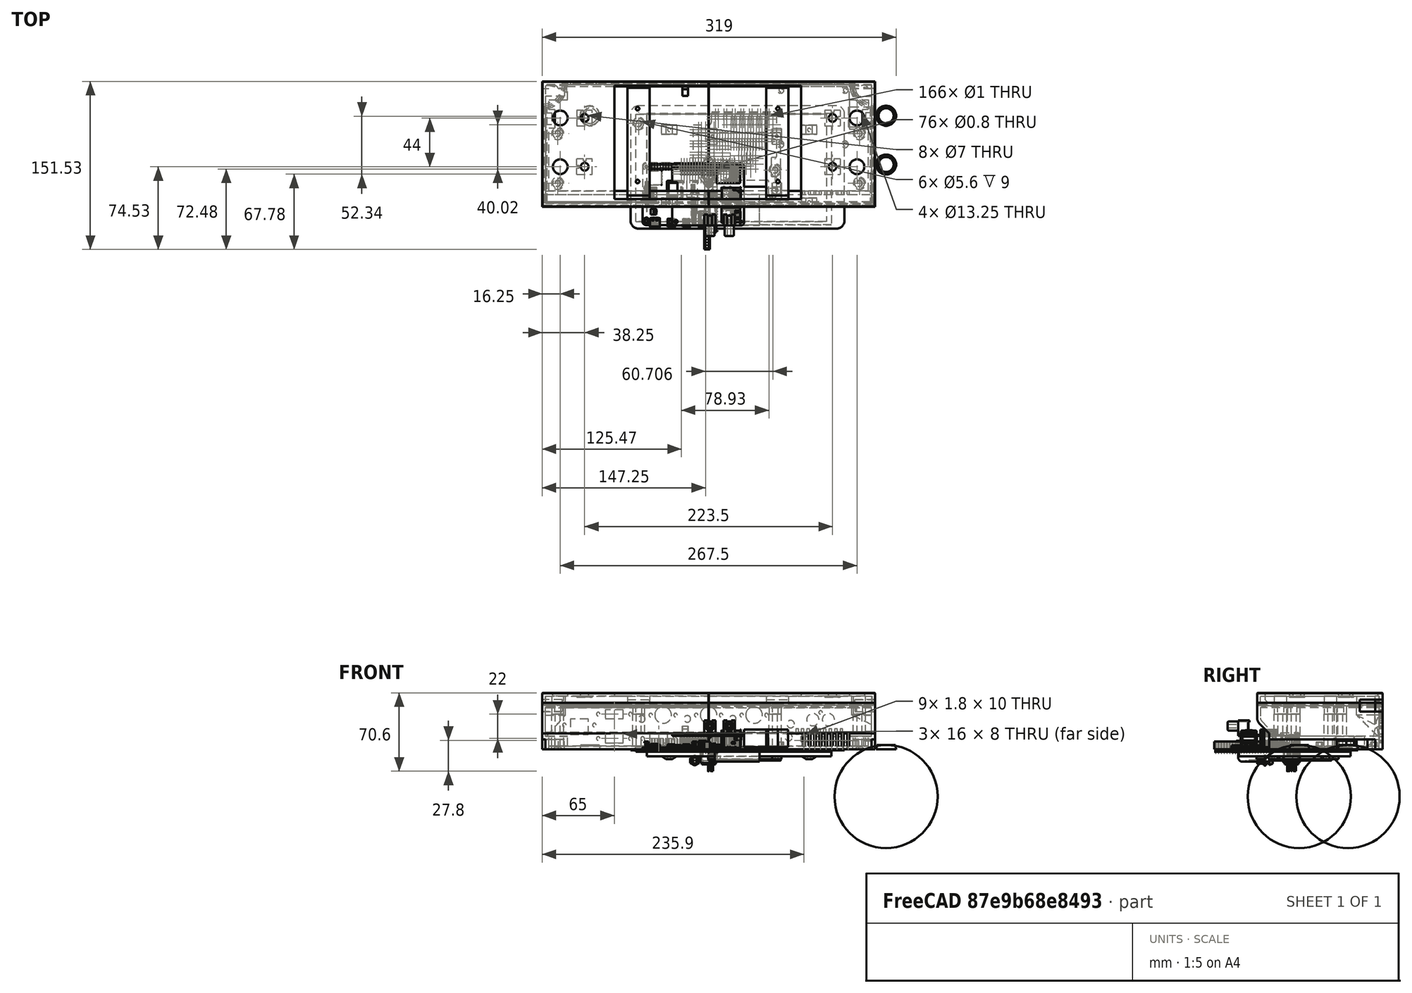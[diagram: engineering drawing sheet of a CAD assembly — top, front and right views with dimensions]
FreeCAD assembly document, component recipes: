
FREECAD ASSEMBLY — COMPONENT RECIPES ("MyZynthian-Boutique")

This assembly document has 19 components, labeled P0..P18 below (a component is one placed body or linked part). 12 of them carry a construction recipe — the FreeCAD feature program that regenerates the part from scratch, quoted from this document or its linked companion documents; the rest are supplied as boundary geometry only. No exploded tour is included for this assembly.
COMPONENT P0 — recipe-attached ("Body Bottom", modeled in this document).
Construction recipe (the document's own serialized feature program — sketch geometry with constraints, then the solid features built on it; lengths are millimeters unless a unit is written):

FEATURE [Sketcher::SketchObject] Sketch002
  FullyConstrained = true
  MapMode = 5
  Placement = pos=(0,0,0) rot=(0.57735,0.57735,0.57735;2.0944rad)
  Support = -> [YZ_Plane037]
  sketch-geometry (8):
    g0: LineSegment StartX=0 StartY=0 StartZ=0 EndX=102 EndY=0 EndZ=0
    g1: LineSegment StartX=102 StartY=0 StartZ=0 EndX=102 EndY=42 EndZ=0
    g2: LineSegment StartX=102 StartY=42 StartZ=0 EndX=-11 EndY=42 EndZ=0
    g3: LineSegment StartX=-11 StartY=42 StartZ=0 EndX=-11 EndY=28.3995 EndZ=0
    g4: LineSegment StartX=-8.94975 StartY=23.4497 StartZ=0 EndX=0 EndY=14.5 EndZ=0
    g5: LineSegment StartX=0 StartY=14.5 StartZ=0 EndX=0 EndY=0 EndZ=0
    g6: ArcOfCircle CenterX=-4 CenterY=28.3995 CenterZ=0 NormalX=0 NormalY=0 NormalZ=1 AngleXU=0 Radius=7 StartAngle=3.14159 EndAngle=3.92699
    g7: GeomPoint X=-11 Y=25.5 Z=0
  constraints (21):
    c: Coincident(g-1,g0)
    c: PointOnObject(g0,g-1)
    c: Coincident(g0,g1)
    c: Vertical(g1)
    c: Horizontal(g2)
    c: Coincident(g2,g3)
    c: Vertical(g3)
    c: PointOnObject(g4,g-2)
    c: Coincident(g4,g5)
    c: Coincident(g5,g0)
    c: DistanceX(g0,g0) = 102
    c: DistanceY(g1,g1) = 42
    c: DistanceY(g5,g5) = 14.5
    c: Angle(g4,g5) = 2.35619
    c: DistanceX(g2,g1) = 113
    c: PointOnObject(g7,g3)
    c: PointOnObject(g7,g4)
    c: Tangent(g3,g6) = -1.5708
    c: Tangent(g4,g6) = -1.5708
    c: Radius(g6) = 7
    c: Coincident(g2,g1)
FEATURE [PartDesign::Pad] Pad001  label="Base"
  Direction = (1,-2e-16,3e-16)
  Length = 300
  Length2 = 10
  Midplane = true
  Placement = pos=(0,0,0) rot=(0.57735,0.57735,0.57735;2.0944rad)
  Profile = -> Sketch002
  ReferenceAxis = -> Sketch002 [N_Axis]
  Type = 0
FEATURE [Sketcher::SketchObject] Sketch003
  ExternalGeometry = -> [Pad001]
  FullyConstrained = true
  MapMode = 5
  Placement = pos=(0,0,4e-16) rot=(0.707107,0.707107,0;3.14159rad)
  Support = -> [Pad001]
  sketch-geometry (20):
    g0: LineSegment StartX=95.5 StartY=130 StartZ=0 EndX=88.5 EndY=130 EndZ=0
    g1: LineSegment StartX=88.5 StartY=130 StartZ=0 EndX=88.5 EndY=147 EndZ=0
    g2: LineSegment StartX=88.5 StartY=147 StartZ=0 EndX=73.5 EndY=147 EndZ=0
    g3: LineSegment StartX=73.5 StartY=147 StartZ=0 EndX=73.5 EndY=141.5 EndZ=0
    g4: LineSegment StartX=73.5 StartY=141.5 StartZ=0 EndX=63 EndY=141.5 EndZ=0
    g5: LineSegment StartX=63 StartY=141.5 StartZ=0 EndX=63 EndY=147 EndZ=0
    g6: LineSegment StartX=63 StartY=147 StartZ=0 EndX=-2.84e-14 EndY=147 EndZ=0
    g7: LineSegment StartX=-2.84e-14 StartY=147 StartZ=0 EndX=-3.21e-14 EndY=150 EndZ=0
    g8: LineSegment StartX=-3.21e-14 StartY=150 StartZ=0 EndX=95.5 EndY=150 EndZ=0
    g9: LineSegment StartX=95.5 StartY=150 StartZ=0 EndX=95.5 EndY=130 EndZ=0
    g10: LineSegment StartX=95.5 StartY=-130 StartZ=0 EndX=88.5 EndY=-130 EndZ=0
    g11: LineSegment StartX=88.5 StartY=-130 StartZ=0 EndX=88.5 EndY=-147 EndZ=0
    g12: LineSegment StartX=88.5 StartY=-147 StartZ=0 EndX=73.5 EndY=-147 EndZ=0
    g13: LineSegment StartX=73.5 StartY=-147 StartZ=0 EndX=73.5 EndY=-141.5 EndZ=0
    g14: LineSegment StartX=73.5 StartY=-141.5 StartZ=0 EndX=63 EndY=-141.5 EndZ=0
    g15: LineSegment StartX=63 StartY=-141.5 StartZ=0 EndX=63 EndY=-147 EndZ=0
    g16: LineSegment StartX=63 StartY=-147 StartZ=0 EndX=3.55e-14 EndY=-147 EndZ=0
    g17: LineSegment StartX=3.55e-14 StartY=-147 StartZ=0 EndX=3.37e-14 EndY=-150 EndZ=0
    g18: LineSegment StartX=3.37e-14 StartY=-150 StartZ=0 EndX=95.5 EndY=-150 EndZ=0
    g19: LineSegment StartX=95.5 StartY=-150 StartZ=0 EndX=95.5 EndY=-130 EndZ=0
  constraints (58):
    c: Coincident(g0,g1)
    c: Horizontal(g2)
    c: Coincident(g2,g3)
    c: Coincident(g3,g4)
    c: Horizontal(g4)
    c: Coincident(g4,g5)
    c: Vertical(g5)
    c: Coincident(g5,g6)
    c: PointOnObject(g6,g-5)
    c: Horizontal(g6)
    c: Coincident(g6,g7)
    c: Vertical(g3)
    c: Vertical(g1)
    c: Horizontal(g0)
    c: DistanceY(g7,g7) = 3
    c: Horizontal(g5,g2)
    c: DistanceX(g5,g2) = 10.5
    c: Coincident(g8,g7)
    c: Horizontal(g8)
    c: DistanceX(g2,g-4) = 28.5
    c: DistanceY(g5,g5) = 5.5
    c: Coincident(g7,g-5)
    c: DistanceY(g0,g8) = 20
    c: DistanceX(g8,g-4) = 6.5
    c: DistanceX(g0,g0) = 7
    c: Coincident(g1,g2)
    c: Coincident(g8,g9)
    c: Vertical(g9)
    c: Coincident(g10,g11)
    c: Horizontal(g12)
    c: Coincident(g12,g13)
    c: Coincident(g13,g14)
    c: Horizontal(g14)
    c: Coincident(g14,g15)
    c: Vertical(g15)
    c: Coincident(g15,g16)
    c: Horizontal(g16)
    c: Coincident(g16,g17)
    c: Vertical(g13)
    c: Vertical(g11)
    c: Horizontal(g10)
    c: Coincident(g18,g17)
    c: Horizontal(g18)
    c: Coincident(g11,g12)
    c: Coincident(g18,g19)
    c: Vertical(g19)
    c: Coincident(g17,g-6)
    c: PointOnObject(g16,g-5)
    c: Vertical(g18,g8)
    c: Vertical(g14,g4)
    c: Vertical(g3,g13)
    c: Equal(g17,g7)
    c: Vertical(g10,g0)
    c: Horizontal(g12,g15)
    c: Equal(g13,g3)
    c: Equal(g11,g1)
    c: Coincident(g9,g0)
    c: Coincident(g10,g19)
FEATURE [PartDesign::Pocket] Pocket  label="Buttom Cutouts"
  BaseFeature = -> Pad001
  Direction = (-4e-16,6e-16,1)
  Length = 8.9
  Length2 = 5
  Placement = pos=(0,0,0) rot=(0.57735,0.57735,0.57735;2.0944rad)
  Profile = -> Sketch003
  ReferenceAxis = -> Sketch003 [N_Axis]
  Type = 0
FEATURE [Sketcher::SketchObject] Sketch004
  ExternalGeometry = -> [Pocket]
  FullyConstrained = true
  MapMode = 5
  Placement = pos=(-1.18e-14,1.85e-14,42) rot=(0,0,-1;1.5708rad)
  Support = -> [Pocket]
  sketch-geometry (8):
    g0: LineSegment StartX=-95.5 StartY=132 StartZ=0 EndX=-102 EndY=132 EndZ=0
    g1: LineSegment StartX=-102 StartY=132 StartZ=0 EndX=-102 EndY=150 EndZ=0
    g2: LineSegment StartX=-102 StartY=150 StartZ=0 EndX=-81.5 EndY=150 EndZ=0
    g3: ArcOfCircle CenterX=-100.071 CenterY=150 CenterZ=0 NormalX=0 NormalY=0 NormalZ=1 AngleXU=0 Radius=18.5714 StartAngle=4.9611 EndAngle=6.28319
    g4: LineSegment StartX=-95.5 StartY=-132 StartZ=0 EndX=-102 EndY=-132 EndZ=0
    g5: LineSegment StartX=-102 StartY=-132 StartZ=0 EndX=-102 EndY=-150 EndZ=0
    g6: LineSegment StartX=-102 StartY=-150 StartZ=0 EndX=-81.5 EndY=-150 EndZ=0
    g7: ArcOfCircle CenterX=-100.071 CenterY=-150 CenterZ=0 NormalX=0 NormalY=0 NormalZ=1 AngleXU=0 Radius=18.5714 StartAngle=0 EndAngle=1.32209
  constraints (22):
    c: PointOnObject(g0,g-4)
    c: Horizontal(g0)
    c: Coincident(g0,g1)
    c: Coincident(g1,g-4)
    c: Coincident(g1,g2)
    c: PointOnObject(g2,g-3)
    c: Perpendicular(g2,g3) = 1.5708
    c: Coincident(g3,g0)
    c: DistanceY(g1,g1) = 18
    c: DistanceX(g0,g0) = 6.5
    c: DistanceX(g0,g2) = 14
    c: PointOnObject(g4,g-4)
    c: Horizontal(g4)
    c: Coincident(g4,g5)
    c: Coincident(g5,g-5)
    c: Coincident(g5,g6)
    c: PointOnObject(g6,g-5)
    c: Perpendicular(g6,g7) = 1.5708
    c: Coincident(g7,g4)
    c: Equal(g1,g5)
    c: Vertical(g0,g4)
    c: Vertical(g2,g6)
FEATURE [PartDesign::Pocket] Pocket001  label="Edge Cutouts001"
  BaseFeature = -> Pocket
  Direction = (7e-16,-7e-16,-1)
  Length = 8
  Length2 = 5
  Placement = pos=(0,0,0) rot=(0.57735,0.57735,0.57735;2.0944rad)
  Profile = -> Sketch004
  ReferenceAxis = -> Sketch004 [N_Axis]
  Type = 0
FEATURE [PartDesign::Thickness] Thickness
  Base = -> Pocket001 [Face26]
  BaseFeature = -> Pocket001
  Intersection = false
  Join = 1
  Mode = 0
  Reversed = true
  SupportTransform = false
  Value = 3
FEATURE [Sketcher::SketchObject] Sketch014  label="Bottom Edge Helper Sketch"
  ExternalGeometry = -> [Thickness]
  FullyConstrained = true
  MapMode = 5
  Placement = pos=(-1.18e-14,1.85e-14,42) rot=(0,0,1;0rad)
  Support = -> [Thickness]
  sketch-geometry (8):
    g0: LineSegment StartX=-150 StartY=81.5 StartZ=0 EndX=-150 EndY=-11 EndZ=0
    g1: LineSegment StartX=-150 StartY=-11 StartZ=0 EndX=150 EndY=-11 EndZ=0
    g2: LineSegment StartX=150 StartY=-11 StartZ=0 EndX=150 EndY=81.5 EndZ=0
    g3: ArcOfCircle CenterX=150 CenterY=100.071 CenterZ=0 NormalX=0 NormalY=0 NormalZ=1 AngleXU=0 Radius=18.5714 StartAngle=3.3903 EndAngle=4.71239
    g4: LineSegment StartX=132 StartY=95.5 StartZ=0 EndX=132 EndY=102 EndZ=0
    g5: LineSegment StartX=132 StartY=102 StartZ=0 EndX=-132 EndY=102 EndZ=0
    g6: LineSegment StartX=-132 StartY=102 StartZ=0 EndX=-132 EndY=95.5 EndZ=0
    g7: ArcOfCircle CenterX=-150 CenterY=100.071 CenterZ=0 NormalX=0 NormalY=0 NormalZ=1 AngleXU=0 Radius=18.5714 StartAngle=4.71239 EndAngle=6.03448
  constraints (16):
    c: Coincident(g-6,g0)
    c: Coincident(g0,g-7)
    c: Coincident(g0,g1)
    c: Coincident(g1,g-10)
    c: Coincident(g1,g2)
    c: Coincident(g2,g-10)
    c: Perpendicular(g2,g3) = 4.71239
    c: Coincident(g3,g-9)
    c: Coincident(g3,g4)
    c: Coincident(g4,g-8)
    c: Coincident(g4,g5)
    c: Coincident(g5,g-4)
    c: Coincident(g5,g6)
    c: Coincident(g6,g-5)
    c: Perpendicular(g0,g7) = 1.5708
    c: Coincident(g7,g6)
FEATURE [Sketcher::SketchObject] Sketch018
  ExternalGeometry = -> [Thickness]
  FullyConstrained = true
  MapMode = 5
  Placement = pos=(0,0,4e-16) rot=(1,0,0;3.14159rad)
  Support = -> [Thickness]
  sketch-geometry (4):
    g0: ArcOfCircle CenterX=139.7 CenterY=-94 CenterZ=0 NormalX=0 NormalY=0 NormalZ=1 AngleXU=0 Radius=4.5 StartAngle=3.48143 EndAngle=5.94335
    g1: LineSegment StartX=135.457 StartY=-95.5 StartZ=0 EndX=143.943 EndY=-95.5 EndZ=0
    g2: ArcOfCircle CenterX=-139.7 CenterY=-94 CenterZ=0 NormalX=0 NormalY=0 NormalZ=1 AngleXU=0 Radius=4.5 StartAngle=3.48143 EndAngle=5.94335
    g3: LineSegment StartX=-143.943 StartY=-95.5 StartZ=0 EndX=-135.457 EndY=-95.5 EndZ=0
  constraints (14):
    c: PointOnObject(g0,g-3)
    c: PointOnObject(g0,g-3)
    c: Radius(g0) = 4.5
    c: DistanceX(g0,g-4) = 10.3
    c: DistanceY(g-5,g0) = 8
    c: Coincident(g1,g0)
    c: Coincident(g1,g0)
    c: PointOnObject(g2,g-7)
    c: PointOnObject(g2,g-7)
    c: Horizontal(g2,g0)
    c: Equal(g0,g2)
    c: DistanceX(g-6,g2) = 10.3
    c: Coincident(g3,g2)
    c: Coincident(g3,g2)
FEATURE [Sketcher::SketchObject] Sketch019
  ExternalGeometry = -> [Thickness]
  FullyConstrained = true
  MapMode = 5
  Placement = pos=(-8e-16,1.3e-15,3) rot=(0,0,1;0rad)
  Support = -> [Thickness]
  sketch-geometry (8):
    g0: LineSegment StartX=-147 StartY=98.5 StartZ=0 EndX=-127 EndY=98.5 EndZ=0
    g1: LineSegment StartX=-127 StartY=98.5 StartZ=0 EndX=-127 EndY=99 EndZ=0
    g2: LineSegment StartX=-127 StartY=99 StartZ=0 EndX=-147 EndY=99 EndZ=0
    g3: LineSegment StartX=-147 StartY=99 StartZ=0 EndX=-147 EndY=98.5 EndZ=0
    g4: LineSegment StartX=127 StartY=98.5 StartZ=0 EndX=147 EndY=98.5 EndZ=0
    g5: LineSegment StartX=147 StartY=98.5 StartZ=0 EndX=147 EndY=99 EndZ=0
    g6: LineSegment StartX=147 StartY=99 StartZ=0 EndX=127 EndY=99 EndZ=0
    g7: LineSegment StartX=127 StartY=99 StartZ=0 EndX=127 EndY=98.5 EndZ=0
  constraints (20):
    c: Coincident(g0,g1)
    c: Coincident(g1,g2)
    c: Coincident(g2,g3)
    c: Coincident(g3,g0)
    c: Horizontal(g2)
    c: Vertical(g1)
    c: Vertical(g3)
    c: Coincident(g0,g-4)
    c: PointOnObject(g1,g-5)
    c: Coincident(g0,g-3)
    c: Coincident(g4,g5)
    c: Coincident(g5,g6)
    c: Coincident(g6,g7)
    c: Coincident(g7,g4)
    c: Horizontal(g4)
    c: Horizontal(g6)
    c: Vertical(g5)
    c: Vertical(g7)
    c: Coincident(g4,g-6)
    c: Coincident(g5,g-7)
FEATURE [PartDesign::Pad] Pad010  label="BottomGapFill"
  BaseFeature = -> Thickness
  Direction = (-1.1e-15,8e-16,1)
  Length = 9
  Length2 = 10
  Profile = -> Sketch019
  ReferenceAxis = -> Sketch019 [N_Axis]
  Type = 0
FEATURE [PartDesign::Pocket] Pocket005  label="Bottom Cutout Screwhole"
  BaseFeature = -> Pad010
  Direction = (-1.1e-15,8e-16,1)
  Length = 8.9
  Length2 = 5
  Profile = -> Sketch018
  ReferenceAxis = -> Sketch018 [N_Axis]
  Type = 0
FEATURE [Sketcher::SketchObject] Sketch020  label="LeftCutout Sketch"
  ExternalGeometry = -> [Pocket005]
  FullyConstrained = true
  MapMode = 5
  Placement = pos=(-2.26e-14,2.23e-14,31) rot=(1,0,0;3.14159rad)
  Support = -> [Pocket005]
  sketch-geometry (4):
    g0: LineSegment StartX=-129 StartY=-95.1392 StartZ=0 EndX=-129 EndY=-99 EndZ=0
    g1: LineSegment StartX=-129 StartY=-99 StartZ=0 EndX=-147 EndY=-99 EndZ=0
    g2: LineSegment StartX=-147 StartY=-99 StartZ=0 EndX=-147 EndY=-78.7096 EndZ=0
    g3: ArcOfCircle CenterX=-150 CenterY=-100.071 CenterZ=0 NormalX=0 NormalY=0 NormalZ=1 AngleXU=0 Radius=21.5714 StartAngle=0.230685 EndAngle=1.43127
  constraints (9):
    c: Coincident(g-6,g0)
    c: Coincident(g0,g-5)
    c: Coincident(g0,g1)
    c: Coincident(g1,g-4)
    c: Coincident(g1,g2)
    c: Coincident(g2,g-6)
    c: Coincident(g3,g0)
    c: Coincident(g3,g2)
    c: Equal(g3,g-6)
FEATURE [Sketcher::SketchObject] Sketch021  label="RightCutout Sketch"
  ExternalGeometry = -> [Pocket005]
  FullyConstrained = true
  MapMode = 5
  Placement = pos=(-2.26e-14,2.23e-14,31) rot=(1,0,0;3.14159rad)
  Support = -> [Pocket005]
  sketch-geometry (4):
    g0: LineSegment StartX=129 StartY=-95.1392 StartZ=0 EndX=129 EndY=-99 EndZ=0
    g1: LineSegment StartX=129 StartY=-99 StartZ=0 EndX=147 EndY=-99 EndZ=0
    g2: LineSegment StartX=147 StartY=-99 StartZ=0 EndX=147 EndY=-78.7096 EndZ=0
    g3: ArcOfCircle CenterX=150 CenterY=-100.071 CenterZ=0 NormalX=0 NormalY=0 NormalZ=1 AngleXU=0 Radius=21.5714 StartAngle=1.71032 EndAngle=2.91091
  constraints (9):
    c: Coincident(g-6,g0)
    c: Coincident(g0,g-6)
    c: Coincident(g0,g1)
    c: Coincident(g1,g-4)
    c: Coincident(g1,g2)
    c: Coincident(g2,g-5)
    c: Coincident(g3,g0)
    c: Coincident(g3,g2)
    c: Equal(g-5,g3)
FEATURE [Sketcher::SketchObject] Sketch022
  ExternalGeometry = -> [Pocket005]
  FullyConstrained = true
  MapMode = 5
  Placement = pos=(-147,3.23e-14,-3.23e-14) rot=(0.57735,0.57735,0.57735;2.0944rad)
  Support = -> [Pocket005]
  sketch-geometry (2):
    g0: LineSegment StartX=99 StartY=31 StartZ=0 EndX=99 EndY=10.7096 EndZ=0
    g1: LineSegment StartX=78.7096 StartY=31 StartZ=0 EndX=99 EndY=31 EndZ=0
  constraints (5):
    c: Coincident(g0,g-3)
    c: PointOnObject(g0,g-3)
    c: Coincident(g1,g-4)
    c: Coincident(g1,g0)
    c: Equal(g0,g1)
FEATURE [PartDesign::AdditiveLoft] AdditiveLoft  label="LeftCutoutSupport"
  BaseFeature = -> Pocket005
  Closed = false
  Profile = -> Sketch022 [Vertex3]
  Ruled = false
  Sections = -> [Sketch020]
FEATURE [Sketcher::SketchObject] Sketch023
  ExternalGeometry = -> [Sketch021,AdditiveLoft]
  FullyConstrained = true
  MapMode = 5
  Placement = pos=(147,-3.23e-14,3.23e-14) rot=(-0.57735,0.57735,0.57735;4.18879rad)
  Support = -> [AdditiveLoft]
  sketch-geometry (2):
    g0: LineSegment StartX=-95.1392 StartY=42 StartZ=0 EndX=-95.1392 EndY=22.228 EndZ=0
    g1: LineSegment StartX=-95.1392 StartY=42 StartZ=0 EndX=-78.7096 EndY=31 EndZ=0
  constraints (5):
    c: Coincident(g0,g-4)
    c: PointOnObject(g0,g-4)
    c: Coincident(g1,g0)
    c: Coincident(g1,g-3)
    c: Equal(g1,g0)
FEATURE [PartDesign::AdditiveLoft] AdditiveLoft001  label="RightCutoutSupport"
  BaseFeature = -> AdditiveLoft
  Closed = false
  Profile = -> Sketch023 [Vertex3]
  Ruled = false
  Sections = -> [Sketch021]
FEATURE [Sketcher::SketchObject] Sketch024
  ExternalGeometry = -> [AdditiveLoft001]
  FullyConstrained = true
  MapMode = 5
  Placement = pos=(0,0,0) rot=(0.57735,0.57735,0.57735;2.0944rad)
  Support = -> [YZ_Plane037]
  sketch-geometry (4):
    g0: LineSegment StartX=-8 StartY=37.6 StartZ=0 EndX=-6.6 EndY=39 EndZ=0
    g1: LineSegment StartX=-6.6 StartY=39 StartZ=0 EndX=-6.6 EndY=42 EndZ=0
    g2: LineSegment StartX=-6.6 StartY=42 StartZ=0 EndX=-8 EndY=42 EndZ=0
    g3: LineSegment StartX=-8 StartY=42 StartZ=0 EndX=-8 EndY=37.6 EndZ=0
  constraints (11):
    c: PointOnObject(g0,g-3)
    c: Coincident(g0,g1)
    c: Coincident(g1,g2)
    c: Coincident(g2,g-3)
    c: Coincident(g2,g3)
    c: Coincident(g3,g0)
    c: Horizontal(g2)
    c: Vertical(g1)
    c: Angle(g0,g3) = 0.785398
    c: DistanceY(g1,g1) = 3
    c: DistanceX(g-4,g1) = 4.4
FEATURE [PartDesign::AdditivePipe] AdditivePipe  label="TopRim"
  AuxilleryCurvelinear = true
  AuxillerySpineTangent = false
  BaseFeature = -> AdditiveLoft001
  Binormal = (0,0,0)
  Mode = 0
  Profile = -> Sketch024
  Spine = -> AdditiveLoft001 [Edge104,Edge103,Edge102,Edge101,Edge108,Edge107,Edge106,Edge105]
  SpineTangent = false
  Transformation = 1
  Transition = 1
FEATURE [Sketcher::SketchObject] Sketch031
  FullyConstrained = true
  MapMode = 5
  Placement = pos=(0,1e-15,0) rot=(1,0,0;1.5708rad)
  sketch-geometry (44):
    g0: LineSegment StartX=125 StartY=13.2 StartZ=0 EndX=126.8 EndY=13.2 EndZ=0
    g1: LineSegment StartX=126.8 StartY=13.2 StartZ=0 EndX=126.8 EndY=3.2 EndZ=0
    g2: LineSegment StartX=126.8 StartY=3.2 StartZ=0 EndX=125 EndY=3.2 EndZ=0
    g3: LineSegment StartX=125 StartY=3.2 StartZ=0 EndX=125 EndY=13.2 EndZ=0
    g4: LineSegment StartX=120 StartY=13.2 StartZ=0 EndX=121.8 EndY=13.2 EndZ=0
    g5: LineSegment StartX=120 StartY=3.2 StartZ=0 EndX=120 EndY=13.2 EndZ=0
    g6: LineSegment StartX=121.8 StartY=13.2 StartZ=0 EndX=121.8 EndY=3.2 EndZ=0
    g7: LineSegment StartX=121.8 StartY=3.2 StartZ=0 EndX=120 EndY=3.2 EndZ=0
    g8: LineSegment StartX=125 StartY=13.2 StartZ=0 EndX=120 EndY=13.2 EndZ=0
    g9: LineSegment StartX=115 StartY=13.2 StartZ=0 EndX=116.8 EndY=13.2 EndZ=0
    g10: LineSegment StartX=115 StartY=3.2 StartZ=0 EndX=115 EndY=13.2 EndZ=0
    g11: LineSegment StartX=116.8 StartY=13.2 StartZ=0 EndX=116.8 EndY=3.2 EndZ=0
    g12: LineSegment StartX=116.8 StartY=3.2 StartZ=0 EndX=115 EndY=3.2 EndZ=0
    g13: LineSegment StartX=120 StartY=13.2 StartZ=0 EndX=115 EndY=13.2 EndZ=0
    g14: LineSegment StartX=110 StartY=13.2 StartZ=0 EndX=111.8 EndY=13.2 EndZ=0
    g15: LineSegment StartX=110 StartY=3.2 StartZ=0 EndX=110 EndY=13.2 EndZ=0
    g16: LineSegment StartX=111.8 StartY=13.2 StartZ=0 EndX=111.8 EndY=3.2 EndZ=0
    g17: LineSegment StartX=111.8 StartY=3.2 StartZ=0 EndX=110 EndY=3.2 EndZ=0
    g18: LineSegment StartX=115 StartY=13.2 StartZ=0 EndX=110 EndY=13.2 EndZ=0
    g19: LineSegment StartX=105 StartY=13.2 StartZ=0 EndX=106.8 EndY=13.2 EndZ=0
    g20: LineSegment StartX=105 StartY=3.2 StartZ=0 EndX=105 EndY=13.2 EndZ=0
    g21: LineSegment StartX=106.8 StartY=13.2 StartZ=0 EndX=106.8 EndY=3.2 EndZ=0
    g22: LineSegment StartX=106.8 StartY=3.2 StartZ=0 EndX=105 EndY=3.2 EndZ=0
    g23: LineSegment StartX=110 StartY=13.2 StartZ=0 EndX=105 EndY=13.2 EndZ=0
    g24: LineSegment StartX=100 StartY=13.2 StartZ=0 EndX=101.8 EndY=13.2 EndZ=0
    g25: LineSegment StartX=100 StartY=3.2 StartZ=0 EndX=100 EndY=13.2 EndZ=0
    g26: LineSegment StartX=101.8 StartY=13.2 StartZ=0 EndX=101.8 EndY=3.2 EndZ=0
    g27: LineSegment StartX=101.8 StartY=3.2 StartZ=0 EndX=100 EndY=3.2 EndZ=0
    g28: LineSegment StartX=105 StartY=13.2 StartZ=0 EndX=100 EndY=13.2 EndZ=0
    g29: LineSegment StartX=95 StartY=13.2 StartZ=0 EndX=96.8 EndY=13.2 EndZ=0
    g30: LineSegment StartX=95 StartY=3.2 StartZ=0 EndX=95 EndY=13.2 EndZ=0
    g31: LineSegment StartX=96.8 StartY=13.2 StartZ=0 EndX=96.8 EndY=3.2 EndZ=0
    g32: LineSegment StartX=96.8 StartY=3.2 StartZ=0 EndX=95 EndY=3.2 EndZ=0
    g33: LineSegment StartX=100 StartY=13.2 StartZ=0 EndX=95 EndY=13.2 EndZ=0
    g34: LineSegment StartX=90 StartY=13.2 StartZ=0 EndX=91.8 EndY=13.2 EndZ=0
    g35: LineSegment StartX=90 StartY=3.2 StartZ=0 EndX=90 EndY=13.2 EndZ=0
    g36: LineSegment StartX=91.8 StartY=13.2 StartZ=0 EndX=91.8 EndY=3.2 EndZ=0
    g37: LineSegment StartX=91.8 StartY=3.2 StartZ=0 EndX=90 EndY=3.2 EndZ=0
    g38: LineSegment StartX=95 StartY=13.2 StartZ=0 EndX=90 EndY=13.2 EndZ=0
    g39: LineSegment StartX=85 StartY=13.2 StartZ=0 EndX=86.8 EndY=13.2 EndZ=0
    g40: LineSegment StartX=86.8 StartY=13.2 StartZ=0 EndX=86.8 EndY=3.2 EndZ=0
    g41: LineSegment StartX=86.8 StartY=3.2 StartZ=0 EndX=85 EndY=3.2 EndZ=0
    g42: LineSegment StartX=85 StartY=3.2 StartZ=0 EndX=85 EndY=13.2 EndZ=0
    g43: LineSegment StartX=85 StartY=13.2 StartZ=0 EndX=90 EndY=13.2 EndZ=0
  constraints (124):
    c: Coincident(g0,g1)
    c: Coincident(g1,g2)
    c: Coincident(g2,g3)
    c: Coincident(g3,g0)
    c: Horizontal(g0)
    c: Horizontal(g2)
    c: Vertical(g1)
    c: Vertical(g3)
    c: DistanceX(g0,g0) = 1.8
    c: DistanceY(g1,g1) = 10
    c: Coincident(g4,g6)
    c: Coincident(g6,g7)
    c: Coincident(g7,g5)
    c: Coincident(g5,g4)
    c: Horizontal(g4)
    c: Horizontal(g7)
    c: Vertical(g6)
    c: Vertical(g5)
    c: Coincident(g0,g8)
    c: Coincident(g4,g8)
    c: Distance(g8) = 5
    c: Angle(g8) = 3.14159
    c: Coincident(g9,g11)
    c: Coincident(g11,g12)
    c: Coincident(g12,g10)
    c: Coincident(g10,g9)
    c: Horizontal(g9)
    c: Horizontal(g12)
    c: Vertical(g11)
    c: Vertical(g10)
    c: Coincident(g4,g13)
    c: Coincident(g9,g13)
    c: Equal(g8,g13)
    c: Parallel(g13,g8)
    c: Coincident(g14,g16)
    c: Coincident(g16,g17)
    c: Coincident(g17,g15)
    c: Coincident(g15,g14)
    c: Horizontal(g14)
    c: Horizontal(g17)
    c: Vertical(g16)
    c: Vertical(g15)
    c: Coincident(g9,g18)
    c: Coincident(g14,g18)
    c: Equal(g8,g18)
    c: Parallel(g18,g8)
    c: Coincident(g19,g21)
    c: Coincident(g21,g22)
    c: Coincident(g22,g20)
    c: Coincident(g20,g19)
    c: Horizontal(g19)
    c: Horizontal(g22)
    c: Vertical(g21)
    c: Vertical(g20)
    c: Coincident(g14,g23)
    c: Coincident(g19,g23)
    c: Equal(g8,g23)
    c: Parallel(g23,g8)
    c: Coincident(g24,g26)
    c: Coincident(g26,g27)
    c: Coincident(g27,g25)
    c: Coincident(g25,g24)
    c: Horizontal(g24)
    c: Horizontal(g27)
    c: Vertical(g26)
    c: Vertical(g25)
    c: Coincident(g19,g28)
    c: Coincident(g24,g28)
    c: Equal(g8,g28)
    c: Parallel(g28,g8)
    c: Coincident(g29,g31)
    c: Coincident(g31,g32)
    c: Coincident(g32,g30)
    c: Coincident(g30,g29)
    c: Horizontal(g29)
    c: Horizontal(g32)
    c: Vertical(g31)
    c: Vertical(g30)
    c: Coincident(g24,g33)
    c: Coincident(g29,g33)
    c: Equal(g8,g33)
    c: Parallel(g33,g8)
    c: Coincident(g34,g36)
    c: Coincident(g36,g37)
    c: Coincident(g37,g35)
    c: Coincident(g35,g34)
    c: Horizontal(g34)
    c: Horizontal(g37)
    c: Vertical(g36)
    c: Vertical(g35)
    c: Coincident(g29,g38)
    c: Coincident(g34,g38)
    c: Equal(g8,g38)
    c: Parallel(g38,g8)
    c: DistanceY(g-1,g35) = 3.2
    c: DistanceX(g-1,g35) = 90
    c: Coincident(g39,g40)
    c: Coincident(g40,g41)
    c: Coincident(g41,g42)
    c: Coincident(g42,g39)
    c: Horizontal(g39)
    c: Horizontal(g41)
    c: Vertical(g40)
    c: Vertical(g42)
    c: Horizontal(g41,g35)
    c: Coincident(g43,g39)
    c: Coincident(g43,g34)
    c: Equal(g0,g4)
    c: Equal(g4,g9)
    c: Equal(g9,g14)
    c: Equal(g14,g19)
    c: Equal(g19,g24)
    c: Equal(g24,g29)
    c: Equal(g29,g34)
    c: Equal(g34,g39)
    c: Horizontal(g30,g36)
    c: Horizontal(g36,g25)
    c: Horizontal(g25,g20)
    c: Horizontal(g20,g15)
    c: Horizontal(g15,g10)
    c: Horizontal(g10,g5)
    c: Horizontal(g5,g2)
    c: Horizontal(g43)
    c: Equal(g43,g38)
FEATURE [PartDesign::SubShapeBinder] Binder  label="Top Screwpost Sketch Binder"
  BindCopyOnChange = 0
  BindMode = 0
  ClaimChildren = false
  Context = -> Body [Binder.]
  Fuse = false
  MakeFace = true
  OffsetFill = false
  OffsetIntersection = false
  OffsetJoinType = 0
  OffsetOpenResult = false
  PartialLoad = false
  Relative = true
  Support = -> [Body006[Sketch033.]]
  _Version = 2
FEATURE [Sketcher::SketchObject] Sketch037
  ExternalGeometry = -> [Binder]
  FullyConstrained = true
  MapMode = 11
  Placement = pos=(-63,64,32) rot=(0.707107,0.707107,0;3.14159rad)
  Support = -> [Binder]
  sketch-geometry (6):
    g0: Circle CenterX=0 CenterY=0 CenterZ=0 NormalX=0 NormalY=0 NormalZ=1 AngleXU=0 Radius=5.5
    g1: Circle CenterX=-9 CenterY=-73 CenterZ=0 NormalX=0 NormalY=0 NormalZ=1 AngleXU=0 Radius=5.5
    g2: Circle CenterX=-42 CenterY=123 CenterZ=0 NormalX=0 NormalY=0 NormalZ=1 AngleXU=0 Radius=5.5
    g3: Circle CenterX=-9 CenterY=199 CenterZ=0 NormalX=0 NormalY=0 NormalZ=1 AngleXU=0 Radius=5.5
    g4: Circle CenterX=-54 CenterY=199 CenterZ=0 NormalX=0 NormalY=0 NormalZ=1 AngleXU=0 Radius=5.5
    g5: Circle CenterX=-54 CenterY=-73 CenterZ=0 NormalX=0 NormalY=0 NormalZ=1 AngleXU=0 Radius=5.5
  constraints (12):
    c: Coincident(g0,g-3)
    c: Coincident(g4,g-8)
    c: Equal(g3,g-6)
    c: Equal(g2,g-5)
    c: Equal(g4,g-8)
    c: Equal(g0,g-3)
    c: Equal(g1,g-4)
    c: Equal(g5,g-7)
    c: Coincident(g5,g-7)
    c: Coincident(g-4,g1)
    c: Coincident(g3,g-6)
    c: Coincident(g-5,g2)
FEATURE [PartDesign::Plane] DatumPlane004  label="Backplanesupport Plane"
  AttachmentOffset = pos=(0,0,-21) rot=(0,0,1;0rad)
  Length = 145.449
  MapMode = 5
  Placement = pos=(-21,4.7e-15,-4.7e-15) rot=(0.57735,0.57735,0.57735;2.0944rad)
  ResizeMode = 0
  Support = -> [YZ_Plane037]
  Width = 85.4488
FEATURE [PartDesign::Body] Body  label="Body Bottom"
  Group = -> [Sketch002,Pad001,Sketch003,Pocket,Sketch004,Pocket001,Thickness,Sketch014,Sketch018,Sketch019,Pad010,Pocket005,Sketch020,Sketch021,Sketch022,AdditiveLoft,Sketch023,AdditiveLoft001,Sketch024,AdditivePipe,Boolean,Sketch025,Pocket006,Sketch026,Pad011,Sketch027,Pocket007,Sketch028,Pad012,Sketch029,Pocket008,Sketch031,Pocket009,Binder,Sketch037,Pad015,Sketch038,Hole,DatumPlane004,Sketch042,Pad018]
  Origin = -> Origin037
  Tip = -> Pad018
FEATURE [PartDesign::Boolean] Boolean  label="TopCover Rim Cutout"
  BaseFeature = -> AdditivePipe
  Group = -> [Body013]
  Type = 1
FEATURE [Sketcher::SketchObject] Sketch025
  ExternalGeometry = -> [Boolean]
  FullyConstrained = true
  MapMode = 5
  Placement = pos=(-1.18e-14,1.85e-14,42) rot=(0,0,1;0rad)
  Support = -> [Boolean]
  sketch-geometry (32):
    g0: LineSegment StartX=-148.5 StartY=80.0636 StartZ=0 EndX=-148.5 EndY=-9.5 EndZ=0
    g1: LineSegment StartX=-148.5 StartY=-9.5 StartZ=0 EndX=148.5 EndY=-9.5 EndZ=0
    g2: LineSegment StartX=148.5 StartY=-9.5 StartZ=0 EndX=148.5 EndY=80.0636 EndZ=0
    g3: LineSegment StartX=130.5 StartY=95.3476 StartZ=0 EndX=130.5 EndY=100.5 EndZ=0
    g4: LineSegment StartX=130.5 StartY=100.5 StartZ=0 EndX=-130.5 EndY=100.5 EndZ=0
    g5: LineSegment StartX=-130.5 StartY=100.5 StartZ=0 EndX=-130.5 EndY=95.3476 EndZ=0
    g6: ArcOfCircle CenterX=150 CenterY=100.071 CenterZ=0 NormalX=0 NormalY=0 NormalZ=1 AngleXU=0 Radius=20.064 StartAngle=3.37926 EndAngle=4.63756
    g7: ArcOfCircle CenterX=-150 CenterY=100.071 CenterZ=0 NormalX=0 NormalY=0 NormalZ=1 AngleXU=0 Radius=20.064 StartAngle=4.78722 EndAngle=6.04551
    g8: LineSegment StartX=-146.95 StartY=78.6531 StartZ=0 EndX=-146.95 EndY=-7.95 EndZ=0
    g9: LineSegment StartX=-146.95 StartY=-7.95 StartZ=0 EndX=-73.1 EndY=-7.95 EndZ=0
    g10: LineSegment StartX=-73.1 StartY=-7.95 StartZ=0 EndX=-73.1 EndY=-6.6 EndZ=0
    g11: LineSegment StartX=-73.1 StartY=-6.6 StartZ=0 EndX=-52.9 EndY=-6.6 EndZ=0
    g12: LineSegment StartX=-52.9 StartY=-6.6 StartZ=0 EndX=-52.9 EndY=-7.95 EndZ=0
    g13: LineSegment StartX=-52.9 StartY=-7.95 StartZ=0 EndX=51.9 EndY=-7.95 EndZ=0
    g14: LineSegment StartX=51.9 StartY=-7.95 StartZ=0 EndX=51.9 EndY=-6.6 EndZ=0
    g15: LineSegment StartX=51.9 StartY=-6.6 StartZ=0 EndX=72.1 EndY=-6.6 EndZ=0
    g16: LineSegment StartX=72.1 StartY=-6.6 StartZ=0 EndX=72.1 EndY=-7.95 EndZ=0
    g17: LineSegment StartX=72.1 StartY=-7.95 StartZ=0 EndX=146.95 EndY=-7.95 EndZ=0
    g18: LineSegment StartX=146.95 StartY=-7.95 StartZ=0 EndX=146.95 EndY=78.6531 EndZ=0
    g19: ArcOfCircle CenterX=-150 CenterY=100.071 CenterZ=0 NormalX=0 NormalY=0 NormalZ=1 AngleXU=0 Radius=21.6344 StartAngle=4.85384 EndAngle=6.05023
    g20: ArcOfCircle CenterX=150 CenterY=100.071 CenterZ=0 NormalX=0 NormalY=0 NormalZ=1 AngleXU=0 Radius=21.6344 StartAngle=3.37454 EndAngle=4.57094
    g21: LineSegment StartX=128.95 StartY=95.0771 StartZ=0 EndX=128.95 EndY=98.95 EndZ=0
    g22: LineSegment StartX=128.95 StartY=98.95 StartZ=0 EndX=72.1 EndY=98.95 EndZ=0
    g23: LineSegment StartX=72.1 StartY=98.95 StartZ=0 EndX=72.1 EndY=97.6 EndZ=0
    g24: LineSegment StartX=72.1 StartY=97.6 StartZ=0 EndX=51.9 EndY=97.6 EndZ=0
    g25: LineSegment StartX=51.9 StartY=97.6 StartZ=0 EndX=51.9 EndY=98.95 EndZ=0
    g26: LineSegment StartX=51.9 StartY=98.95 StartZ=0 EndX=-52.9 EndY=98.95 EndZ=0
    g27: LineSegment StartX=-52.9 StartY=98.95 StartZ=0 EndX=-52.9 EndY=97.6 EndZ=0
    g28: LineSegment StartX=-52.9 StartY=97.6 StartZ=0 EndX=-73.1 EndY=97.6 EndZ=0
    g29: LineSegment StartX=-73.1 StartY=97.6 StartZ=0 EndX=-73.1 EndY=98.95 EndZ=0
    g30: LineSegment StartX=-73.1 StartY=98.95 StartZ=0 EndX=-128.95 EndY=98.95 EndZ=0
    g31: LineSegment StartX=-128.95 StartY=98.95 StartZ=0 EndX=-128.95 EndY=95.0771 EndZ=0
  constraints (96):
    c: Vertical(g0)
    c: Coincident(g0,g1)
    c: Horizontal(g1)
    c: Coincident(g1,g2)
    c: Vertical(g2)
    c: Vertical(g3)
    c: Coincident(g3,g4)
    c: Horizontal(g4)
    c: Coincident(g4,g5)
    c: Vertical(g5)
    c: Coincident(g6,g3)
    c: Coincident(g6,g2)
    c: Coincident(g7,g5)
    c: Coincident(g7,g0)
    c: DistanceY(g-5,g4) = 0.1
    c: DistanceY(g-9,g0) = 0.1
    c: Coincident(g-7,g7)
    c: DistanceX(g4,g-5) = 0.1
    c: DistanceX(g-5,g3) = 0.1
    c: Coincident(g6,g-22)
    c: DistanceY(g-20,g2) = 0.1
    c: DistanceX(g-20,g2) = 0.1
    c: DistanceY(g1,g-19) = 0.1
    c: DistanceX(g0,g-10) = 0.1
    c: Vertical(g8)
    c: Coincident(g8,g9)
    c: Horizontal(g9)
    c: Coincident(g9,g10)
    c: Coincident(g10,g11)
    c: Horizontal(g11)
    c: Coincident(g11,g12)
    c: Coincident(g12,g13)
    c: Coincident(g13,g14)
    c: Coincident(g14,g15)
    c: Horizontal(g15)
    c: Coincident(g15,g16)
    c: Coincident(g16,g17)
    c: Horizontal(g17)
    c: Coincident(g17,g18)
    c: Vertical(g18)
    c: Horizontal(g11,g14)
    c: Vertical(g12)
    c: Vertical(g14)
    c: Vertical(g10)
    c: Horizontal(g12,g9)
    c: Horizontal(g10,g-12)
    c: Horizontal(g13)
    c: DistanceX(g14,g-15) = 0.1
    c: DistanceX(g-16,g15) = 0.1
    c: Vertical(g16)
    c: Horizontal(g16,g13)
    c: DistanceX(g17,g-18) = 0.1
    c: DistanceX(g10,g-12) = 0.1
    c: DistanceX(g-13,g11) = 0.1
    c: DistanceX(g-11,g8) = 0.1
    c: DistanceY(g-11,g8) = 0.1
    c: Coincident(g19,g8)
    c: Coincident(g20,g18)
    c: Coincident(g21,g22)
    c: Horizontal(g22)
    c: Coincident(g22,g23)
    c: Vertical(g23)
    c: Coincident(g23,g24)
    c: Horizontal(g24)
    c: Coincident(g24,g25)
    c: Vertical(g25)
    c: Coincident(g25,g26)
    c: Horizontal(g26)
    c: Coincident(g26,g27)
    c: Vertical(g27)
    c: Coincident(g27,g28)
    c: Horizontal(g28)
    c: Coincident(g28,g29)
    c: Vertical(g29)
    c: Coincident(g29,g30)
    c: Horizontal(g30)
    c: Coincident(g30,g31)
    c: Coincident(g31,g19)
    c: Vertical(g31)
    c: Coincident(g19,g7)
    c: DistanceY(g8,g-8) = 0.1
    c: DistanceX(g-6,g30) = 0.1
    c: DistanceY(g30,g-6) = 0.1
    c: Horizontal(g26,g29)
    c: Horizontal(g28,g-28)
    c: Horizontal(g24,g-25)
    c: Horizontal(g22,g25)
    c: Vertical(g21)
    c: DistanceY(g18,g-22) = 0.1
    c: DistanceX(g21,g-23) = 0.1
    c: Coincident(g21,g20)
    c: Coincident(g6,g20)
    c: DistanceX(g-24,g23) = 0.1
    c: DistanceX(g24,g-25) = 0.1
    c: DistanceX(g-27,g27) = 0.1
    c: DistanceX(g28,g-28) = 0.1
FEATURE [PartDesign::Pocket] Pocket006  label="TopCover Rim Clearance Cutout"
  BaseFeature = -> Boolean
  Direction = (3e-16,-4e-16,-1)
  Length = 2.1
  Length2 = 5
  Profile = -> Sketch025
  ReferenceAxis = -> Sketch025 [N_Axis]
  Type = 0
FEATURE [Sketcher::SketchObject] Sketch026
  ExternalGeometry = -> [Pocket006]
  FullyConstrained = true
  MapMode = 5
  Placement = pos=(-8e-16,1.3e-15,3) rot=(0,0,1;0rad)
  Support = -> [Pocket006]
  sketch-geometry (8):
    g0: LineSegment StartX=144 StartY=76.5 StartZ=0 EndX=144 EndY=85.5 EndZ=0
    g1: LineSegment StartX=144 StartY=85.5 StartZ=0 EndX=127 EndY=85.5 EndZ=0
    g2: LineSegment StartX=127 StartY=85.5 StartZ=0 EndX=127 EndY=59 EndZ=0
    g3: LineSegment StartX=127 StartY=59 StartZ=0 EndX=144 EndY=59 EndZ=0
    g4: LineSegment StartX=144 StartY=59 StartZ=0 EndX=144 EndY=60 EndZ=0
    g5: LineSegment StartX=144 StartY=60 StartZ=0 EndX=138.5 EndY=60 EndZ=0
    g6: LineSegment StartX=138.5 StartY=60 StartZ=0 EndX=138.5 EndY=76.5 EndZ=0
    g7: LineSegment StartX=138.5 StartY=76.5 StartZ=0 EndX=144 EndY=76.5 EndZ=0
  constraints (21):
    c: Coincident(g0,g1)
    c: Horizontal(g1)
    c: Coincident(g1,g2)
    c: Vertical(g2)
    c: Coincident(g2,g3)
    c: Horizontal(g3)
    c: Coincident(g3,g4)
    c: Coincident(g4,g5)
    c: Coincident(g5,g6)
    c: Coincident(g6,g7)
    c: Coincident(g7,g0)
    c: DistanceY(g4,g4) = 1
    c: DistanceX(g1,g1) = 17
    c: Vertical(g4)
    c: Coincident(g0,g-3)
    c: Vertical(g0)
    c: Coincident(g6,g-4)
    c: Coincident(g5,g-4)
    c: Horizontal(g5)
    c: Horizontal(g7)
    c: Vertical(g4,g0)
FEATURE [PartDesign::Pad] Pad011  label="SDCard Pad"
  BaseFeature = -> Pocket006
  Direction = (-3e-16,4e-16,1)
  Length = 9
  Length2 = 10
  Profile = -> Sketch026
  ReferenceAxis = -> Sketch026 [N_Axis]
  Type = 0
FEATURE [Sketcher::SketchObject] Sketch027
  ExternalGeometry = -> [Pad011]
  FullyConstrained = true
  MapMode = 5
  Placement = pos=(0,0,4e-16) rot=(1,0,0;3.14159rad)
  Support = -> [Pad011]
  sketch-geometry (9):
    g0: Circle CenterX=123 CenterY=-94.2 CenterZ=0 NormalX=0 NormalY=0 NormalZ=1 AngleXU=0 Radius=1.55
    g1: Circle CenterX=123 CenterY=-45.2 CenterZ=0 NormalX=0 NormalY=0 NormalZ=1 AngleXU=0 Radius=1.55
    g2: Circle CenterX=65 CenterY=-45.2 CenterZ=0 NormalX=0 NormalY=0 NormalZ=1 AngleXU=0 Radius=1.55
    g3: Circle CenterX=65 CenterY=-94.2 CenterZ=0 NormalX=0 NormalY=0 NormalZ=1 AngleXU=0 Radius=1.55
    g4: LineSegment StartX=126 StartY=-60.8 StartZ=0 EndX=150 EndY=-60.8 EndZ=0
    g5: LineSegment StartX=150 StartY=-60.8 StartZ=0 EndX=150 EndY=-78.8 EndZ=0
    g6: LineSegment StartX=150 StartY=-78.8 StartZ=0 EndX=126 EndY=-78.8 EndZ=0
    g7: LineSegment StartX=126 StartY=-78.8 StartZ=0 EndX=126 EndY=-60.8 EndZ=0
    g8: GeomPoint X=150 Y=-69.8 Z=0
  constraints (25):
    c: Horizontal(g2,g1)
    c: Horizontal(g0,g3)
    c: Vertical(g2,g3)
    c: Vertical(g0,g1)
    c: DistanceX(g2,g1) = 58
    c: DistanceY(g3,g2) = 49
    c: Coincident(g4,g5)
    c: Coincident(g5,g6)
    c: Coincident(g6,g7)
    c: Coincident(g7,g4)
    c: Horizontal(g4)
    c: Horizontal(g6)
    c: Vertical(g5)
    c: Vertical(g7)
    c: DistanceX(g4,g4) = 24
    c: DistanceY(g7,g7) = 18
    c: Symmetric(g5,g4,g8)
    c: Diameter(g2) = 3.1
    c: Equal(g2,g3)
    c: Equal(g3,g0)
    c: Equal(g0,g1)
    c: Vertical(g-3,g8)
    c: DistanceY(g-3,g0) = 7.8
    c: DistanceY(g0,g8) = 24.4
    c: DistanceX(g0,g-3) = 27
FEATURE [PartDesign::Pocket] Pocket007  label="RPi Mount Bottom Cutout"
  BaseFeature = -> Pad011
  Direction = (-3e-16,4e-16,1)
  Length = 7.7
  Length2 = 5
  Profile = -> Sketch027
  ReferenceAxis = -> Sketch027 [N_Axis]
  Type = 0
FEATURE [Sketcher::SketchObject] Sketch028
  ExternalGeometry = -> [Pocket007]
  FullyConstrained = true
  MapMode = 5
  Placement = pos=(-8e-16,1.3e-15,3) rot=(0,0,1;0rad)
  Support = -> [Pocket007]
  sketch-geometry (8):
    g0: Circle CenterX=65 CenterY=94.2 CenterZ=0 NormalX=0 NormalY=0 NormalZ=1 AngleXU=0 Radius=1.55
    g1: Circle CenterX=65 CenterY=94.2 CenterZ=0 NormalX=0 NormalY=0 NormalZ=1 AngleXU=0 Radius=2.95
    g2: Circle CenterX=65 CenterY=45.2 CenterZ=0 NormalX=0 NormalY=0 NormalZ=1 AngleXU=0 Radius=1.55
    g3: Circle CenterX=65 CenterY=45.2 CenterZ=0 NormalX=0 NormalY=0 NormalZ=1 AngleXU=0 Radius=2.95
    g4: Circle CenterX=123 CenterY=45.2 CenterZ=0 NormalX=0 NormalY=0 NormalZ=1 AngleXU=0 Radius=1.55
    g5: Circle CenterX=123 CenterY=45.2 CenterZ=0 NormalX=0 NormalY=0 NormalZ=1 AngleXU=0 Radius=2.95
    g6: Circle CenterX=123 CenterY=94.2 CenterZ=0 NormalX=0 NormalY=0 NormalZ=1 AngleXU=0 Radius=1.55
    g7: Circle CenterX=123 CenterY=94.2 CenterZ=0 NormalX=0 NormalY=0 NormalZ=1 AngleXU=0 Radius=2.95
  constraints (16):
    c: Coincident(g1,g0)
    c: Coincident(g3,g2)
    c: Coincident(g5,g4)
    c: Coincident(g7,g6)
    c: Equal(g1,g7)
    c: Equal(g7,g5)
    c: Equal(g5,g3)
    c: Diameter(g3) = 5.9
    c: Equal(g2,g4)
    c: Equal(g4,g0)
    c: Equal(g0,g6)
    c: Coincident(g-3,g0)
    c: Equal(g0,g-3)
    c: Coincident(g-4,g2)
    c: Coincident(g-5,g4)
    c: Coincident(g-6,g6)
FEATURE [PartDesign::Pad] Pad012  label="RPi Posts"
  BaseFeature = -> Pocket007
  Direction = (-3e-16,4e-16,1)
  Length = 3.5
  Length2 = 10
  Profile = -> Sketch028
  ReferenceAxis = -> Sketch028 [N_Axis]
  Type = 0
FEATURE [Sketcher::SketchObject] Sketch029
  ExternalGeometry = -> [Pad012]
  FullyConstrained = true
  MapMode = 5
  Placement = pos=(4.49e-14,102,-2.24e-14) rot=(0,0.707107,0.707107;3.14159rad)
  Support = -> [Pad012]
  sketch-geometry (117):
    g0: Circle CenterX=-41 CenterY=31 CenterZ=0 NormalX=0 NormalY=0 NormalZ=1 AngleXU=0 Radius=7.5
    g1: Circle CenterX=0 CenterY=31 CenterZ=0 NormalX=0 NormalY=0 NormalZ=1 AngleXU=0 Radius=7.5
    g2: Circle CenterX=41 CenterY=31 CenterZ=0 NormalX=0 NormalY=0 NormalZ=1 AngleXU=0 Radius=7.5
    g3: Circle CenterX=-52.2 CenterY=31 CenterZ=0 NormalX=0 NormalY=0 NormalZ=1 AngleXU=0 Radius=1.6
    g4: Circle CenterX=-29.8 CenterY=31 CenterZ=0 NormalX=0 NormalY=0 NormalZ=1 AngleXU=0 Radius=1.6
    g5: Circle CenterX=-11.2 CenterY=31 CenterZ=0 NormalX=0 NormalY=0 NormalZ=1 AngleXU=0 Radius=1.6
    g6: Circle CenterX=11.2 CenterY=31 CenterZ=0 NormalX=0 NormalY=0 NormalZ=1 AngleXU=0 Radius=1.6
    g7: Circle CenterX=29.8 CenterY=31 CenterZ=0 NormalX=0 NormalY=0 NormalZ=1 AngleXU=0 Radius=1.6
    g8: Circle CenterX=-21.8 CenterY=27.5 CenterZ=0 NormalX=0 NormalY=0 NormalZ=1 AngleXU=0 Radius=3
    g9: Circle CenterX=19.2 CenterY=27.5 CenterZ=0 NormalX=0 NormalY=0 NormalZ=1 AngleXU=0 Radius=3
    g10: Circle CenterX=60.2 CenterY=27.5 CenterZ=0 NormalX=0 NormalY=0 NormalZ=1 AngleXU=0 Radius=3
    g11: Circle CenterX=52.2 CenterY=31 CenterZ=0 NormalX=0 NormalY=0 NormalZ=1 AngleXU=0 Radius=1.6
    g12: Circle CenterX=-108 CenterY=26.8 CenterZ=0 NormalX=0 NormalY=0 NormalZ=1 AngleXU=0 Radius=5.5
    g13: Circle CenterX=-94 CenterY=26.8 CenterZ=0 NormalX=0 NormalY=0 NormalZ=1 AngleXU=0 Radius=5.5
    g14: Circle CenterX=-74 CenterY=22.8 CenterZ=0 NormalX=0 NormalY=0 NormalZ=1 AngleXU=0 Radius=3.35
    g15: Circle CenterX=-72.2 CenterY=11 CenterZ=0 NormalX=0 NormalY=0 NormalZ=1 AngleXU=0 Radius=3.25
    g16: Circle CenterX=-101 CenterY=33.3 CenterZ=0 NormalX=0 NormalY=0 NormalZ=1 AngleXU=0 Radius=1.6
    g17: LineSegment StartX=-101 StartY=26.8 StartZ=0 EndX=-101 EndY=33.3 EndZ=0
    g18: LineSegment StartX=-119.75 StartY=11.7 StartZ=0 EndX=-110.25 EndY=11.7 EndZ=0
    g19: LineSegment StartX=-110.25 StartY=11.7 StartZ=0 EndX=-110.25 EndY=7.5 EndZ=0
    g20: LineSegment StartX=-110.25 StartY=7.5 StartZ=0 EndX=-119.75 EndY=7.5 EndZ=0
    g21: LineSegment StartX=-119.75 StartY=7.5 StartZ=0 EndX=-119.75 EndY=11.7 EndZ=0
    g22: LineSegment StartX=-103.9 StartY=11.7 StartZ=0 EndX=-96.5 EndY=11.7 EndZ=0
    g23: LineSegment StartX=-96.5 StartY=11.7 StartZ=0 EndX=-96.5 EndY=7.2 EndZ=0
    g24: LineSegment StartX=-96.5 StartY=7.2 StartZ=0 EndX=-103.9 EndY=7.2 EndZ=0
    g25: LineSegment StartX=-103.9 StartY=7.2 StartZ=0 EndX=-103.9 EndY=11.7 EndZ=0
    g26: LineSegment StartX=-90.4 StartY=11.7 StartZ=0 EndX=-83 EndY=11.7 EndZ=0
    g27: LineSegment StartX=-83 StartY=11.7 StartZ=0 EndX=-83 EndY=7.2 EndZ=0
    g28: LineSegment StartX=-83 StartY=7.2 StartZ=0 EndX=-90.4 EndY=7.2 EndZ=0
    g29: LineSegment StartX=-90.4 StartY=7.2 StartZ=0 EndX=-90.4 EndY=11.7 EndZ=0
    g30: GeomPoint X=-115 Y=7.5 Z=0
    g31: GeomPoint X=-100.2 Y=7.2 Z=0
    g32: GeomPoint X=-86.7 Y=7.2 Z=0
    g33: GeomPoint X=-123 Y=8 Z=0
    g34: GeomPoint X=-123 Y=19.8 Z=0
    g35: LineSegment StartX=66 StartY=16.7 StartZ=0 EndX=104 EndY=16.7 EndZ=0
    g36: LineSegment StartX=104 StartY=16.7 StartZ=0 EndX=104 EndY=3 EndZ=0
    g37: LineSegment StartX=104 StartY=3 StartZ=0 EndX=66 EndY=3 EndZ=0
    g38: LineSegment StartX=66 StartY=3 StartZ=0 EndX=66 EndY=16.7 EndZ=0
    g39: LineSegment StartX=26 StartY=16.7 StartZ=0 EndX=64 EndY=16.7 EndZ=0
    g40: LineSegment StartX=64 StartY=16.7 StartZ=0 EndX=64 EndY=3 EndZ=0
    g41: LineSegment StartX=64 StartY=3 StartZ=0 EndX=26 EndY=3 EndZ=0
    g42: LineSegment StartX=26 StartY=3 StartZ=0 EndX=26 EndY=16.7 EndZ=0
    g43: LineSegment StartX=98 StartY=33.5 StartZ=0 EndX=135 EndY=33.5 EndZ=0
    g44: LineSegment StartX=135 StartY=33.5 StartZ=0 EndX=135 EndY=10.5 EndZ=0
    g45: LineSegment StartX=135 StartY=10.5 StartZ=0 EndX=98 EndY=10.5 EndZ=0
    g46: LineSegment StartX=98 StartY=10.5 StartZ=0 EndX=98 EndY=33.5 EndZ=0
    g47: Circle CenterX=103 CenterY=22 CenterZ=0 NormalX=0 NormalY=0 NormalZ=1 AngleXU=0 Radius=1.6
    g48: Circle CenterX=130 CenterY=22 CenterZ=0 NormalX=0 NormalY=0 NormalZ=1 AngleXU=0 Radius=1.6
    g49: Circle CenterX=70.5 CenterY=9.85 CenterZ=0 NormalX=0 NormalY=0 NormalZ=1 AngleXU=0 Radius=1.6
    g50: Circle CenterX=99.5 CenterY=9.85 CenterZ=0 NormalX=0 NormalY=0 NormalZ=1 AngleXU=0 Radius=1.6
    g51: Circle CenterX=30.5 CenterY=9.85 CenterZ=0 NormalX=0 NormalY=0 NormalZ=1 AngleXU=0 Radius=1.6
    g52: Circle CenterX=59.5 CenterY=9.85 CenterZ=0 NormalX=0 NormalY=0 NormalZ=1 AngleXU=0 Radius=1.6
    g53: GeomPoint X=45 Y=9.85 Z=0
    g54: GeomPoint X=85 Y=9.85 Z=0
    g55: GeomPoint X=116.5 Y=22 Z=0
    g56: LineSegment StartX=77 StartY=13.85 StartZ=0 EndX=93 EndY=13.85 EndZ=0
    g57: LineSegment StartX=93 StartY=13.85 StartZ=0 EndX=93 EndY=5.85 EndZ=0
    g58: LineSegment StartX=93 StartY=5.85 StartZ=0 EndX=77 EndY=5.85 EndZ=0
    g59: LineSegment StartX=77 StartY=5.85 StartZ=0 EndX=77 EndY=13.85 EndZ=0
    g60: LineSegment StartX=37 StartY=13.85 StartZ=0 EndX=53 EndY=13.85 EndZ=0
    g61: LineSegment StartX=53 StartY=13.85 StartZ=0 EndX=53 EndY=5.85 EndZ=0
    g62: LineSegment StartX=53 StartY=5.85 StartZ=0 EndX=37 EndY=5.85 EndZ=0
    g63: LineSegment StartX=37 StartY=5.85 StartZ=0 EndX=37 EndY=13.85 EndZ=0
    g64: LineSegment StartX=108.5 StartY=27.5 StartZ=0 EndX=124.5 EndY=27.5 EndZ=0
    g65: LineSegment StartX=124.5 StartY=27.5 StartZ=0 EndX=124.5 EndY=13.5 EndZ=0
    g66: LineSegment StartX=124.5 StartY=13.5 StartZ=0 EndX=108.5 EndY=13.5 EndZ=0
    g67: LineSegment StartX=108.5 StartY=13.5 StartZ=0 EndX=108.5 EndY=27.5 EndZ=0
    g68: GeomPoint X=116.5 Y=20.5 Z=0
    g69: LineSegment StartX=132 StartY=34 StartZ=0 EndX=150 EndY=16 EndZ=0
    g70: LineSegment StartX=66 StartY=38.7 StartZ=0 EndX=104 EndY=38.7 EndZ=0
    g71: LineSegment StartX=104 StartY=38.7 StartZ=0 EndX=104 EndY=25 EndZ=0
    g72: LineSegment StartX=104 StartY=25 StartZ=0 EndX=66 EndY=25 EndZ=0
    g73: LineSegment StartX=66 StartY=25 StartZ=0 EndX=66 EndY=38.7 EndZ=0
    g74: Circle CenterX=70.5 CenterY=31.85 CenterZ=0 NormalX=0 NormalY=0 NormalZ=1 AngleXU=0 Radius=1.6
    g75: Circle CenterX=99.5 CenterY=31.85 CenterZ=0 NormalX=0 NormalY=0 NormalZ=1 AngleXU=0 Radius=1.6
    g76: GeomPoint X=85 Y=31.85 Z=0
    g77: LineSegment StartX=77 StartY=35.85 StartZ=0 EndX=93 EndY=35.85 EndZ=0
    g78: LineSegment StartX=93 StartY=35.85 StartZ=0 EndX=93 EndY=27.85 EndZ=0
    g79: LineSegment StartX=93 StartY=27.85 StartZ=0 EndX=77 EndY=27.85 EndZ=0
    g80: LineSegment StartX=77 StartY=27.85 StartZ=0 EndX=77 EndY=35.85 EndZ=0
    g81: LineSegment StartX=-121 StartY=18.7 StartZ=0 EndX=-118.5 EndY=18.7 EndZ=0
    g82: LineSegment StartX=-118.5 StartY=18.7 StartZ=0 EndX=-118.5 EndY=13.7 EndZ=0
    g83: LineSegment StartX=-118.5 StartY=13.7 StartZ=0 EndX=-121 EndY=13.7 EndZ=0
    g84: LineSegment StartX=-121 StartY=13.7 StartZ=0 EndX=-121 EndY=18.7 EndZ=0
    g85: LineSegment StartX=-116 StartY=18.7 StartZ=0 EndX=-113.5 EndY=18.7 EndZ=0
    g86: LineSegment StartX=-113.5 StartY=18.7 StartZ=0 EndX=-113.5 EndY=13.7 EndZ=0
    g87: LineSegment StartX=-113.5 StartY=13.7 StartZ=0 EndX=-116 EndY=13.7 EndZ=0
    g88: LineSegment StartX=-116 StartY=13.7 StartZ=0 EndX=-116 EndY=18.7 EndZ=0
    g89: LineSegment StartX=-111 StartY=18.7 StartZ=0 EndX=-108.5 EndY=18.7 EndZ=0
    g90: LineSegment StartX=-108.5 StartY=18.7 StartZ=0 EndX=-108.5 EndY=13.7 EndZ=0
    g91: LineSegment StartX=-108.5 StartY=13.7 StartZ=0 EndX=-111 EndY=13.7 EndZ=0
    g92: LineSegment StartX=-111 StartY=13.7 StartZ=0 EndX=-111 EndY=18.7 EndZ=0
    g93: LineSegment StartX=-106 StartY=18.7 StartZ=0 EndX=-103.5 EndY=18.7 EndZ=0
    g94: LineSegment StartX=-103.5 StartY=18.7 StartZ=0 EndX=-103.5 EndY=13.7 EndZ=0
    g95: LineSegment StartX=-103.5 StartY=13.7 StartZ=0 EndX=-106 EndY=13.7 EndZ=0
    g96: LineSegment StartX=-106 StartY=13.7 StartZ=0 EndX=-106 EndY=18.7 EndZ=0
    g97: LineSegment StartX=-101 StartY=18.7 StartZ=0 EndX=-98.5 EndY=18.7 EndZ=0
    g98: LineSegment StartX=-98.5 StartY=18.7 StartZ=0 EndX=-98.5 EndY=13.7 EndZ=0
    g99: LineSegment StartX=-98.5 StartY=13.7 StartZ=0 EndX=-101 EndY=13.7 EndZ=0
    g100: LineSegment StartX=-101 StartY=13.7 StartZ=0 EndX=-101 EndY=18.7 EndZ=0
    g101: LineSegment StartX=-96 StartY=18.7 StartZ=0 EndX=-93.5 EndY=18.7 EndZ=0
    g102: LineSegment StartX=-93.5 StartY=18.7 StartZ=0 EndX=-93.5 EndY=13.7 EndZ=0
    g103: LineSegment StartX=-93.5 StartY=13.7 StartZ=0 EndX=-96 EndY=13.7 EndZ=0
    g104: LineSegment StartX=-96 StartY=13.7 StartZ=0 EndX=-96 EndY=18.7 EndZ=0
    g105: LineSegment StartX=-91 StartY=18.7 StartZ=0 EndX=-88.5 EndY=18.7 EndZ=0
    g106: LineSegment StartX=-88.5 StartY=18.7 StartZ=0 EndX=-88.5 EndY=13.7 EndZ=0
    g107: LineSegment StartX=-88.5 StartY=13.7 StartZ=0 EndX=-91 EndY=13.7 EndZ=0
    g108: LineSegment StartX=-91 StartY=13.7 StartZ=0 EndX=-91 EndY=18.7 EndZ=0
    g109: LineSegment StartX=-86 StartY=18.7 StartZ=0 EndX=-83.5 EndY=18.7 EndZ=0
    g110: LineSegment StartX=-83.5 StartY=18.7 StartZ=0 EndX=-83.5 EndY=13.7 EndZ=0
    g111: LineSegment StartX=-83.5 StartY=13.7 StartZ=0 EndX=-86 EndY=13.7 EndZ=0
    g112: LineSegment StartX=-86 StartY=13.7 StartZ=0 EndX=-86 EndY=18.7 EndZ=0
    g113: LineSegment StartX=-81 StartY=18.7 StartZ=0 EndX=-78.5 EndY=18.7 EndZ=0
    g114: LineSegment StartX=-78.5 StartY=18.7 StartZ=0 EndX=-78.5 EndY=13.7 EndZ=0
    g115: LineSegment StartX=-78.5 StartY=13.7 StartZ=0 EndX=-81 EndY=13.7 EndZ=0
    g116: LineSegment StartX=-81 StartY=13.7 StartZ=0 EndX=-81 EndY=18.7 EndZ=0
  constraints (319):
    c: Equal(g0,g1)
    c: Equal(g1,g2)
    c: Diameter(g0) = 15
    c: Equal(g3, g4-g7) x4
    c: Diameter(g3) = 3.2
    c: Equal(g11,g7)
    c: Horizontal(g11,g2)
    c: Horizontal(g7,g6)
    c: Horizontal(g6,g1)
    c: Horizontal(g5,g4)
    c: Horizontal(g4,g0)
    c: Symmetric(g3,g4,g0)
    c: Symmetric(g5,g6,g1)
    c: Symmetric(g7,g11,g2)
    c: DistanceY(g-1,g1) = 31
    c: DistanceX(g3,g4) = 22.4
    c: DistanceX(g5,g6) = 22.4
    c: DistanceX(g7,g11) = 22.4
    c: DistanceX(g0,g1) = 41
    c: DistanceX(g1,g2) = 41
    c: DistanceX(g4,g8) = 8
    c: DistanceX(g6,g9) = 8
    c: DistanceX(g11,g10) = 8
    c: Horizontal(g8,g9)
    c: Horizontal(g9,g10)
    c: DistanceY(g10,g11) = 3.5
    c: PointOnObject(g1,g-2)
    c: Equal(g9,g10)
    c: Equal(g9,g8)
    c: Diameter(g9) = 6
    c: Horizontal(g12,g13)
    c: Diameter(g12) = 11
    c: Equal(g12,g13)
    c: DistanceX(g12,g13) = 14
    c: Coincident(g17,g16)
    c: Vertical(g17)
    c: Symmetric(g12,g13,g17)
    c: DistanceY(g17,g17) = 6.5
    c: Diameter(g16) = 3.2
    c: Diameter(g14) = 6.7
    c: Diameter(g15) = 6.5
    c: Coincident(g18,g19)
    c: Coincident(g19,g20)
    c: Coincident(g20,g21)
    c: Coincident(g21,g18)
    c: Horizontal(g18)
    c: Horizontal(g20)
    c: Vertical(g19)
    c: Vertical(g21)
    c: Coincident(g22,g23)
    c: Coincident(g23,g24)
    c: Coincident(g24,g25)
    c: Coincident(g25,g22)
    c: Horizontal(g22)
    c: Horizontal(g24)
    c: Vertical(g23)
    c: Vertical(g25)
    c: Coincident(g26,g27)
    c: Coincident(g27,g28)
    c: Coincident(g28,g29)
    c: Coincident(g29,g26)
    c: Horizontal(g26)
    c: Horizontal(g28)
    c: Vertical(g27)
    c: Vertical(g29)
    c: Horizontal(g23,g28)
    c: Horizontal(g26,g22)
    c: DistanceY(g21,g21) = 4.2
    c: DistanceY(g27,g27) = 4.5
    c: Symmetric(g20,g19,g30)
    c: Symmetric(g24,g23,g31)
    c: Symmetric(g28,g27,g32)
    c: DistanceX(g-3,g33) = 27
    c: DistanceY(g-3,g33) = 8
    c: DistanceX(g33,g30) = 8
    c: DistanceX(g30,g31) = 14.8
    c: DistanceX(g31,g32) = 13.5
    c: DistanceX(g32,g15) = 14.5
    c: Equal(g26,g22)
    c: DistanceY(g24,g33) = 0.8
    c: DistanceY(g20,g33) = 0.5
    c: DistanceX(g18,g18) = 9.5
    c: DistanceX(g22,g22) = 7.4
    c: DistanceY(g33,g15) = 3
    c: Vertical(g34,g33)
    c: DistanceY(g33,g34) = 11.8
    c: DistanceX(g34,g12) = 15
    c: DistanceX(g34,g14) = 49
    c: DistanceY(g34,g14) = 3
    c: DistanceY(g34,g12) = 7
    c: Coincident(g35,g36)
    c: Coincident(g36,g37)
    c: Coincident(g37,g38)
    c: Coincident(g38,g35)
    c: Horizontal(g35)
    c: Horizontal(g37)
    c: Vertical(g36)
    c: Vertical(g38)
    c: Coincident(g39,g40)
    c: Coincident(g40,g41)
    c: Coincident(g41,g42)
    c: Coincident(g42,g39)
    c: Horizontal(g39)
    c: Horizontal(g41)
    c: Vertical(g40)
    c: Vertical(g42)
    c: DistanceY(g36,g36) = 13.7
    c: DistanceX(g37,g37) = 38
    c: Coincident(g43,g44)
    c: Coincident(g44,g45)
    c: Coincident(g45,g46)
    c: Coincident(g46,g43)
    c: Horizontal(g43)
    c: Horizontal(g45)
    c: Vertical(g44)
    c: Vertical(g46)
    c: DistanceX(g45,g45) = 37
    c: DistanceY(g44,g44) = 23
    c: Equal(g36,g40)
    c: Equal(g35,g41)
    c: Symmetric(g37,g35,g54)
    c: Symmetric(g41,g39,g53)
    c: Symmetric(g49,g50,g54)
    c: Symmetric(g51,g52,g53)
    c: Horizontal(g49,g50)
    c: Horizontal(g51,g52)
    c: Horizontal(g47,g48)
    c: Symmetric(g47,g48,g55)
    c: Equal(g51,g49)
    c: Equal(g51,g52)
    c: Equal(g51,g50)
    c: Equal(g51,g47)
    c: Equal(g51,g48)
    c: Diameter(g51) = 3.2
    c: DistanceX(g49,g50) = 29
    c: DistanceX(g51,g52) = 29
    c: DistanceX(g47,g48) = 27
    c: Coincident(g56,g57)
    c: Coincident(g57,g58)
    c: Coincident(g58,g59)
    c: Coincident(g59,g56)
    c: Horizontal(g56)
    c: Horizontal(g58)
    c: Vertical(g57)
    c: Vertical(g59)
    c: Coincident(g60,g61)
    c: Coincident(g61,g62)
    c: Coincident(g62,g63)
    c: Coincident(g63,g60)
    c: Horizontal(g60)
    c: Horizontal(g62)
    c: Vertical(g61)
    c: Vertical(g63)
    c: Coincident(g64,g65)
    c: Coincident(g65,g66)
    c: Coincident(g66,g67)
    c: Coincident(g67,g64)
    c: Horizontal(g64)
    c: Horizontal(g66)
    c: Vertical(g65)
    c: Vertical(g67)
    c: Symmetric(g62,g60,g53)
    c: Symmetric(g58,g56,g54)
    c: Equal(g57,g61)
    c: Equal(g56,g60)
    c: DistanceX(g58,g58) = 16
    c: DistanceY(g57,g57) = 8
    c: DistanceX(g66,g66) = 16
    c: DistanceY(g67,g67) = 14
    c: DistanceY(g47,g64) = 5.5
    c: Symmetric(g66,g64,g68)
    c: Vertical(g68,g55)
    c: Symmetric(g45,g43,g55)
    c: Coincident(g69,g-5)
    c: Angle(g69,g-5) = 0.785398
    c: Vertical(g69,g-5)
    c: DistanceY(g-4,g36) = 3
    c: DistanceX(g69,g43) = 3
    c: DistanceY(g43,g-6) = 8.5
    c: DistanceX(g45,g35) = 6
    c: Coincident(g70,g71)
    c: Coincident(g71,g72)
    c: Coincident(g72,g73)
    c: Coincident(g73,g70)
    c: Horizontal(g70)
    c: Horizontal(g72)
    c: Vertical(g71)
    c: Vertical(g73)
    c: Symmetric(g72,g70,g76)
    c: Symmetric(g74,g75,g76)
    c: Horizontal(g74,g75)
    c: Equal(g51,g74) = 3.2
    c: DistanceX(g74,g75) = 29
    c: Coincident(g77,g78)
    c: Coincident(g78,g79)
    c: Coincident(g79,g80)
    c: Coincident(g80,g77)
    c: Horizontal(g77)
    c: Horizontal(g79)
    c: Vertical(g78)
    c: Vertical(g80)
    c: Symmetric(g79,g77,g76)
    c: Equal(g71,g36)
    c: Vertical(g35,g72)
    c: Horizontal(g40,g37)
    c: DistanceY(g50,g75) = 22
    c: Equal(g57,g78)
    c: Equal(g56,g77)
    c: Equal(g74,g75)
    c: Equal(g72,g35)
    c: DistanceX(g40,g37) = 2
    c: Coincident(g81,g82)
    c: Coincident(g82,g83)
    c: Coincident(g83,g84)
    c: Coincident(g84,g81)
    c: Horizontal(g81)
    c: Horizontal(g83)
    c: Vertical(g82)
    c: Vertical(g84)
    c: Coincident(g85,g86)
    c: Coincident(g86,g87)
    c: Coincident(g87,g88)
    c: Coincident(g88,g85)
    c: Horizontal(g85)
    c: Horizontal(g87)
    c: Vertical(g86)
    c: Vertical(g88)
    c: Horizontal(g82,g87)
    c: Horizontal(g81,g85)
    c: Equal(g81,g85)
    c: DistanceY(g18,g83) = 2
    c: DistanceY(g84,g84) = 5
    c: DistanceX(g83,g83) = 2.5
    c: DistanceX(g33,g83) = 2
    c: DistanceX(g82,g87) = 2.5
    c: Coincident(g89,g90)
    c: Coincident(g90,g91)
    c: Coincident(g91,g92)
    c: Coincident(g92,g89)
    c: Horizontal(g89)
    c: Horizontal(g91)
    c: Vertical(g90)
    c: Vertical(g92)
    c: Coincident(g93,g94)
    c: Coincident(g94,g95)
    c: Coincident(g95,g96)
    c: Coincident(g96,g93)
    c: Horizontal(g93)
    c: Horizontal(g95)
    c: Vertical(g94)
    c: Vertical(g96)
    c: Coincident(g97,g98)
    c: Coincident(g98,g99)
    c: Coincident(g99,g100)
    c: Coincident(g100,g97)
    c: Horizontal(g97)
    c: Horizontal(g99)
    c: Vertical(g98)
    c: Vertical(g100)
    c: Coincident(g101,g102)
    c: Coincident(g102,g103)
    c: Coincident(g103,g104)
    c: Coincident(g104,g101)
    c: Horizontal(g101)
    c: Horizontal(g103)
    c: Vertical(g102)
    c: Vertical(g104)
    c: Coincident(g105,g106)
    c: Coincident(g106,g107)
    c: Coincident(g107,g108)
    c: Coincident(g108,g105)
    c: Horizontal(g105)
    c: Horizontal(g107)
    c: Vertical(g106)
    c: Vertical(g108)
    c: Coincident(g109,g110)
    c: Coincident(g110,g111)
    c: Coincident(g111,g112)
    c: Coincident(g112,g109)
    c: Horizontal(g109)
    c: Horizontal(g111)
    c: Vertical(g110)
    c: Vertical(g112)
    c: Coincident(g113,g114)
    c: Coincident(g114,g115)
    c: Coincident(g115,g116)
    c: Coincident(g116,g113)
    c: Horizontal(g113)
    c: Horizontal(g115)
    c: Vertical(g114)
    c: Vertical(g116)
    c: Horizontal(g86,g91)
    c: Horizontal(g91,g95)
    c: Horizontal(g95,g99)
    c: Horizontal(g99,g103)
    c: Horizontal(g103,g107)
    c: Horizontal(g107,g111)
    c: Horizontal(g111,g115)
    c: Horizontal(g85,g89)
    c: Horizontal(g89,g93)
    c: Horizontal(g93,g97)
    c: Horizontal(g97,g101)
    c: Horizontal(g101,g105)
    c: Horizontal(g105,g109)
    c: Horizontal(g109,g113)
    c: Equal(g81,g89)
    c: Equal(g89,g93)
    c: Equal(g93,g97)
    c: Equal(g97,g101)
    c: Equal(g101,g105)
    c: Equal(g105,g109)
    c: Equal(g109,g113)
    c: DistanceX(g86,g91) = 2.5
    c: DistanceX(g90,g95) = 2.5
    c: DistanceX(g94,g99) = 2.5
    c: DistanceX(g98,g103) = 2.5
    c: DistanceX(g102,g107) = 2.5
    c: DistanceX(g106,g111) = 2.5
    c: DistanceX(g110,g115) = 2.5
FEATURE [PartDesign::Pocket] Pocket008  label="Back Connector Cutouts"
  BaseFeature = -> Pad012
  Direction = (-4e-16,-1,2e-16)
  Length = 5
  Length2 = 5
  Profile = -> Sketch029
  ReferenceAxis = -> Sketch029 [N_Axis]
  Type = 0
FEATURE [PartDesign::Pocket] Pocket009  label="Airflow Cutouts Front"
  BaseFeature = -> Pocket008
  Direction = (0,1,-2e-16)
  Length = 5
  Length2 = 5
  Profile = -> Sketch031
  ReferenceAxis = -> Sketch031 [N_Axis]
  Type = 0
FEATURE [PartDesign::Pad] Pad015  label="Screwposts"
  BaseFeature = -> Pocket009
  Direction = (0,0,-1)
  Length = 30.9
  Length2 = 10
  Profile = -> Sketch037
  ReferenceAxis = -> Sketch037 [N_Axis]
  Type = 3
  UpToFace = -> Pocket009 [Face135]
FEATURE [Sketcher::SketchObject] Sketch038
  ExternalGeometry = -> [Pad015]
  FullyConstrained = true
  MapMode = 5
  Placement = pos=(0,0,4e-16) rot=(1,0,0;3.14159rad)
  Support = -> [Pad015]
  sketch-geometry (6):
    g0: Circle CenterX=60 CenterY=-22 CenterZ=0 NormalX=0 NormalY=0 NormalZ=1 AngleXU=0 Radius=4
    g1: Circle CenterX=136 CenterY=-55 CenterZ=0 NormalX=0 NormalY=0 NormalZ=1 AngleXU=0 Radius=4
    g2: Circle CenterX=-63 CenterY=-64 CenterZ=0 NormalX=0 NormalY=0 NormalZ=1 AngleXU=0 Radius=4
    g3: Circle CenterX=-136 CenterY=-55 CenterZ=0 NormalX=0 NormalY=0 NormalZ=1 AngleXU=0 Radius=4
    g4: Circle CenterX=-136 CenterY=-10 CenterZ=0 NormalX=0 NormalY=0 NormalZ=1 AngleXU=0 Radius=4
    g5: Circle CenterX=136 CenterY=-10 CenterZ=0 NormalX=0 NormalY=0 NormalZ=1 AngleXU=0 Radius=4
  constraints (12):
    c: Equal(g0,g1)
    c: Equal(g0,g2)
    c: Equal(g0,g3)
    c: Diameter(g0) = 8
    c: Equal(g5,g4)
    c: Equal(g4,g0)
    c: Coincident(g1,g-7)
    c: Coincident(g5,g-8)
    c: Coincident(g0,g-6)
    c: Coincident(g3,g-4)
    c: Coincident(g4,g-3)
    c: Coincident(g2,g-5)
FEATURE [PartDesign::Hole] Hole  label="M4 Screwholes"
  BaseFeature = -> Pad015
  CustomThreadClearance = 0
  Depth = 651.183
  DepthType = 1
  Diameter = 4.4
  DrillForDepth = false
  DrillPoint = 1
  DrillPointAngle = 118
  HoleCutCountersinkAngle = 90
  HoleCutCustomValues = false
  HoleCutDepth = 0
  HoleCutDiameter = 9
  HoleCutType = 2
  ModelThread = false
  Profile = -> Sketch038
  Tapered = false
  TaperedAngle = 90
  ThreadClass = 0
  ThreadDepth = 651.183
  ThreadDepthType = 0
  ThreadDirection = 0
  ThreadFit = 0
  ThreadSize = 0
  ThreadType = 0
  Threaded = false
  UseCustomThreadClearance = false
FEATURE [Sketcher::SketchObject] Sketch042
  ExternalGeometry = -> [Hole]
  FullyConstrained = true
  MapMode = 5
  Placement = pos=(-21,4.7e-15,-4.7e-15) rot=(0.57735,0.57735,0.57735;2.0944rad)
  Support = -> [DatumPlane004]
  sketch-geometry (6):
    g0: LineSegment StartX=99 StartY=3 StartZ=0 EndX=99 EndY=21 EndZ=0
    g1: LineSegment StartX=99 StartY=21 StartZ=0 EndX=95 EndY=18.6906 EndZ=0
    g2: LineSegment StartX=95 StartY=18.6906 StartZ=0 EndX=93.2406 EndY=8.7126 EndZ=0
    g3: ArcOfCircle CenterX=87 CenterY=9.81299 CenterZ=0 NormalX=0 NormalY=0 NormalZ=1 AngleXU=0 Radius=6.33688 StartAngle=5.03349 EndAngle=6.10865
    g4: LineSegment StartX=89 StartY=3.8 StartZ=0 EndX=89 EndY=3 EndZ=0
    g5: LineSegment StartX=89 StartY=3 StartZ=0 EndX=99 EndY=3 EndZ=0
  constraints (17):
    c: Coincident(g-4,g0)
    c: Vertical(g0)
    c: Coincident(g0,g1)
    c: Coincident(g1,g2)
    c: Tangent(g2,g3) = 1.5708
    c: Coincident(g3,g4)
    c: Vertical(g4)
    c: Coincident(g4,g5)
    c: Coincident(g5,g0)
    c: Horizontal(g5)
    c: DistanceY(g0,g0) = 18
    c: DistanceX(g5,g5) = 10
    c: DistanceX(g3,g3) = 2
    c: DistanceY(g4,g4) = 0.8
    c: DistanceX(g1,g0) = 4
    c: Angle(g1,g0) = 1.0472
    c: Angle(g2,g1) = 2.26893
FEATURE [PartDesign::Pad] Pad018  label="Backplane Support"
  BaseFeature = -> Hole
  Direction = (1,-1e-16,1e-16)
  Length = 5
  Length2 = 10
  Midplane = true
  Profile = -> Sketch042
  ReferenceAxis = -> Sketch042 [N_Axis]
  Type = 0
COMPONENT P1 — recipe-attached ("Boutique Sketch", modeled in this document).
Construction recipe (the document's own serialized feature program — sketch geometry with constraints, then the solid features built on it; lengths are millimeters unless a unit is written):

FEATURE [Sketcher::SketchObject] Sketch
  FullyConstrained = true
  MapMode = 5
  Placement = pos=(0,0,0) rot=(0.57735,0.57735,0.57735;2.0944rad)
  Support = -> [YZ_Plane032]
  sketch-geometry (11):
    g0: LineSegment StartX=0 StartY=0 StartZ=0 EndX=102 EndY=0 EndZ=0
    g1: LineSegment StartX=102 StartY=0 StartZ=0 EndX=102 EndY=34.1 EndZ=0
    g2: LineSegment StartX=102 StartY=34.1 StartZ=0 EndX=-13.5 EndY=34.1 EndZ=0
    g3: ArcOfCircle CenterX=-13.5 CenterY=29.1 CenterZ=0 NormalX=0 NormalY=0 NormalZ=1 AngleXU=0 Radius=5 StartAngle=1.5708 EndAngle=3.14159
    g4: LineSegment StartX=-18.5 StartY=29.1 StartZ=0 EndX=-18.5 EndY=27.3 EndZ=0
    g5: LineSegment StartX=0 StartY=14.5 StartZ=0 EndX=0 EndY=0 EndZ=0
    g6: LineSegment StartX=-13.5 StartY=22.3 StartZ=0 EndX=-6.5 EndY=22.3 EndZ=0
    g7: LineSegment StartX=-6.5 StartY=22.3 StartZ=0 EndX=-6.5 EndY=14.5 EndZ=0
    g8: LineSegment StartX=-6.5 StartY=14.5 StartZ=0 EndX=0 EndY=14.5 EndZ=0
    g9: ArcOfCircle CenterX=-13.5 CenterY=27.3 CenterZ=0 NormalX=0 NormalY=0 NormalZ=1 AngleXU=0 Radius=5 StartAngle=3.14159 EndAngle=4.71239
    g10: GeomPoint X=-18.5 Y=22.3 Z=0
  constraints (29):
    c: Coincident(g-1,g0)
    c: PointOnObject(g0,g-1)
    c: Coincident(g0,g1)
    c: Vertical(g1)
    c: Coincident(g1,g2)
    c: Horizontal(g2)
    c: Tangent(g2,g3) = -1.5708
    c: Tangent(g3,g4) = -1.5708
    c: PointOnObject(g5,g-2)
    c: Coincident(g5,g0)
    c: DistanceY(g1,g1) = 34.1
    c: Vertical(g4)
    c: Horizontal(g6)
    c: Coincident(g6,g7)
    c: Vertical(g7)
    c: Coincident(g7,g8)
    c: Coincident(g8,g5)
    c: Horizontal(g8)
    c: DistanceY(g5,g5) = 14.5
    c: DistanceX(g8,g8) = 6.5
    c: DistanceY(g7,g7) = 7.8
    c: DistanceX(g10,g6) = 12
    c: Radius(g3) = 5
    c: PointOnObject(g10,g4)
    c: PointOnObject(g10,g6)
    c: Tangent(g4,g9) = -1.5708
    c: Tangent(g6,g9) = -1.5708
    c: Radius(g9) = 5
    c: DistanceX(g0,g0) = 102
FEATURE [PartDesign::Pad] Pad
  Direction = (1,-2e-16,3e-16)
  Length = 300
  Length2 = 10
  Midplane = true
  Placement = pos=(0,0,0) rot=(0.57735,0.57735,0.57735;2.0944rad)
  Profile = -> Sketch
  ReferenceAxis = -> Sketch [N_Axis]
  Type = 0
FEATURE [PartDesign::Body] Body001  label="Boutique Sketch"
  Group = -> [Sketch,Pad]
  Origin = -> Origin032
  Tip = -> Pad
COMPONENT P2 — recipe-attached ("Top Cover", modeled in this document).
Construction recipe (the document's own serialized feature program — sketch geometry with constraints, then the solid features built on it; lengths are millimeters unless a unit is written):

FEATURE [Sketcher::SketchObject] Sketch005
  FullyConstrained = true
  MapMode = 5
  Placement = pos=(0,0,0) rot=(0.57735,0.57735,0.57735;2.0944rad)
  Support = -> [YZ_Plane038]
  sketch-geometry (4):
    g0: LineSegment StartX=-11 StartY=51 StartZ=0 EndX=102 EndY=51 EndZ=0
    g1: LineSegment StartX=102 StartY=51 StartZ=0 EndX=102 EndY=40 EndZ=0
    g2: LineSegment StartX=102 StartY=40 StartZ=0 EndX=-11 EndY=40 EndZ=0
    g3: LineSegment StartX=-11 StartY=40 StartZ=0 EndX=-11 EndY=51 EndZ=0
  constraints (12):
    c: Coincident(g0,g1)
    c: Coincident(g1,g2)
    c: Coincident(g2,g3)
    c: Coincident(g3,g0)
    c: Horizontal(g0)
    c: Horizontal(g2)
    c: Vertical(g1)
    c: Vertical(g3)
    c: DistanceX(g0,g0) = 113
    c: DistanceX(g-1,g1) = 102
    c: DistanceY(g3,g3) = 11
    c: DistanceY(g-1,g2) = 40
FEATURE [PartDesign::Pad] Pad002
  Direction = (1,-2e-16,3e-16)
  Length = 300
  Length2 = 10
  Midplane = true
  Placement = pos=(0,0,0) rot=(0.57735,0.57735,0.57735;2.0944rad)
  Profile = -> Sketch005
  ReferenceAxis = -> Sketch005 [N_Axis]
  Type = 0
FEATURE [Sketcher::SketchObject] Sketch006
  ExternalGeometry = -> [Pad002]
  FullyConstrained = true
  MapMode = 5
  Placement = pos=(-1.12e-14,1.76e-14,40) rot=(0.707107,0.707107,0;3.14159rad)
  Support = -> [Pad002]
  sketch-geometry (8):
    g0: LineSegment StartX=102 StartY=150 StartZ=0 EndX=81.5 EndY=150 EndZ=0
    g1: ArcOfCircle CenterX=100.071 CenterY=150 CenterZ=0 NormalX=0 NormalY=0 NormalZ=1 AngleXU=0 Radius=18.5714 StartAngle=3.14159 EndAngle=4.46368
    g2: LineSegment StartX=95.5 StartY=132 StartZ=0 EndX=102 EndY=132 EndZ=0
    g3: LineSegment StartX=102 StartY=132 StartZ=0 EndX=102 EndY=150 EndZ=0
    g4: LineSegment StartX=102 StartY=-150 StartZ=0 EndX=81.5 EndY=-150 EndZ=0
    g5: ArcOfCircle CenterX=100.071 CenterY=-150 CenterZ=0 NormalX=0 NormalY=0 NormalZ=1 AngleXU=0 Radius=18.5714 StartAngle=1.81951 EndAngle=3.14159
    g6: LineSegment StartX=95.5 StartY=-132 StartZ=0 EndX=102 EndY=-132 EndZ=0
    g7: LineSegment StartX=102 StartY=-132 StartZ=0 EndX=102 EndY=-150 EndZ=0
  constraints (22):
    c: Coincident(g-4,g0)
    c: PointOnObject(g0,g-3)
    c: Perpendicular(g0,g1) = 1.5708
    c: Coincident(g1,g2)
    c: PointOnObject(g2,g-4)
    c: Horizontal(g2)
    c: Coincident(g2,g3)
    c: Coincident(g3,g0)
    c: Coincident(g-5,g4)
    c: PointOnObject(g4,g-5)
    c: Perpendicular(g4,g5) = 1.5708
    c: Coincident(g5,g6)
    c: PointOnObject(g6,g-4)
    c: Coincident(g6,g7)
    c: Coincident(g7,g4)
    c: Horizontal(g6)
    c: Vertical(g4,g0)
    c: Equal(g3,g7)
    c: DistanceY(g3,g3) = 18
    c: DistanceX(g2,g2) = 6.5
    c: DistanceX(g0,g1) = 14
    c: Vertical(g5,g1)
FEATURE [PartDesign::Pocket] Pocket002  label="Edge Cutouts"
  BaseFeature = -> Pad002
  Direction = (-4e-16,6e-16,1)
  Length = 5
  Length2 = 5
  Placement = pos=(0,0,0) rot=(0.57735,0.57735,0.57735;2.0944rad)
  Profile = -> Sketch006
  ReferenceAxis = -> Sketch006 [N_Axis]
  Type = 0
FEATURE [PartDesign::Thickness] Thickness001
  Base = -> Pocket002 [Face6]
  BaseFeature = -> Pocket002
  Intersection = false
  Join = 1
  Mode = 0
  Reversed = true
  SupportTransform = false
  Value = 2.95
FEATURE [Sketcher::SketchObject] Sketch007
  ExternalGeometry = -> [Thickness001]
  FullyConstrained = true
  MapMode = 5
  Placement = pos=(0,3.3e-14,51) rot=(0,0,1;0rad)
  sketch-geometry (14):
    g0: LineSegment StartX=83.25 StartY=-4 StartZ=0 EndX=-84.75 EndY=-4 EndZ=0
    g1: LineSegment StartX=-84.75 StartY=-4 StartZ=0 EndX=-84.75 EndY=98 EndZ=0
    g2: LineSegment StartX=-84.75 StartY=98 StartZ=0 EndX=83.25 EndY=98 EndZ=0
    g3: LineSegment StartX=83.25 StartY=98 StartZ=0 EndX=83.25 EndY=-4 EndZ=0
    g4: Circle CenterX=-111.75 CenterY=69 CenterZ=0 NormalX=0 NormalY=0 NormalZ=1 AngleXU=0 Radius=3.5
    g5: Circle CenterX=-111.75 CenterY=25 CenterZ=0 NormalX=0 NormalY=0 NormalZ=1 AngleXU=0 Radius=3.5
    g6: Circle CenterX=111.75 CenterY=69 CenterZ=0 NormalX=0 NormalY=0 NormalZ=1 AngleXU=0 Radius=3.5
    g7: Circle CenterX=111.75 CenterY=25 CenterZ=0 NormalX=0 NormalY=0 NormalZ=1 AngleXU=0 Radius=3.5
    g8: Circle CenterX=133.75 CenterY=69 CenterZ=0 NormalX=0 NormalY=0 NormalZ=1 AngleXU=0 Radius=6.625
    g9: Circle CenterX=133.75 CenterY=25 CenterZ=0 NormalX=0 NormalY=0 NormalZ=1 AngleXU=0 Radius=6.625
    g10: Circle CenterX=-133.75 CenterY=25 CenterZ=0 NormalX=0 NormalY=0 NormalZ=1 AngleXU=0 Radius=6.625
    g11: Circle CenterX=-133.75 CenterY=69 CenterZ=0 NormalX=0 NormalY=0 NormalZ=1 AngleXU=0 Radius=6.625
    g12: LineSegment StartX=-96.75 StartY=102 StartZ=0 EndX=-96.75 EndY=-11 EndZ=0
    g13: LineSegment StartX=96.75 StartY=102 StartZ=0 EndX=96.75 EndY=-11 EndZ=0
  constraints (40):
    c: Coincident(g0,g1)
    c: Coincident(g1,g2)
    c: Coincident(g2,g3)
    c: Coincident(g3,g0)
    c: Horizontal(g2)
    c: Vertical(g1)
    c: Vertical(g3)
    c: DistanceX(g2,g2) = 168
    c: DistanceY(g3,g3) = 102
    c: Symmetric(g11,g8,g-2)
    c: Symmetric(g4,g6,g-2)
    c: Symmetric(g5,g7,g-2)
    c: Symmetric(g10,g9,g-2)
    c: Equal(g9,g8)
    c: Equal(g8,g11)
    c: Equal(g11,g10)
    c: Equal(g4,g5)
    c: Equal(g5,g7)
    c: Equal(g7,g6)
    c: Vertical(g10,g11)
    c: Vertical(g5,g4)
    c: Diameter(g4) = 7
    c: Diameter(g11) = 13.25
    c: Horizontal(g0)
    c: Vertical(g12)
    c: Vertical(g13)
    c: DistanceX(g12,g13) = 193.5
    c: Symmetric(g12,g13,g-2)
    c: DistanceX(g12,g0) = 12
    c: DistanceX(g0,g13) = 13.5
    c: DistanceX(g4,g12) = 15
    c: DistanceX(g11,g4) = 22
    c: DistanceY(g10,g11) = 44
    c: DistanceY(g5,g4) = 44
    c: DistanceY(g1,g-4) = 4
    c: PointOnObject(g12,g-3)
    c: PointOnObject(g12,g-5)
    c: PointOnObject(g13,g-3)
    c: DistanceY(g4,g-4) = 33
    c: DistanceY(g11,g-4) = 33
FEATURE [PartDesign::Pocket] Pocket003  label="Frontpanel Cutouts"
  BaseFeature = -> Thickness001
  Direction = (0,0,-1)
  Length = 5
  Length2 = 5
  Profile = -> Sketch007
  ReferenceAxis = -> Sketch007 [N_Axis]
  Type = 1
FEATURE [Sketcher::SketchObject] Sketch008
  ExternalGeometry = -> [Pocket003]
  FullyConstrained = true
  MapMode = 5
  Placement = pos=(-1.35e-14,2.11e-14,48.05) rot=(1,0,0;3.14159rad)
  Support = -> [Pocket003]
  sketch-geometry (52):
    g0: LineSegment StartX=-118.75 StartY=-18 StartZ=0 EndX=-104.75 EndY=-18 EndZ=0
    g1: LineSegment StartX=-104.75 StartY=-18 StartZ=0 EndX=-104.75 EndY=-32 EndZ=0
    g2: LineSegment StartX=-104.75 StartY=-32 StartZ=0 EndX=-110.65 EndY=-32 EndZ=0
    g3: LineSegment StartX=-110.65 StartY=-32 StartZ=0 EndX=-110.65 EndY=-30 EndZ=0
    g4: LineSegment StartX=-110.65 StartY=-30 StartZ=0 EndX=-112.85 EndY=-30 EndZ=0
    g5: LineSegment StartX=-112.85 StartY=-30 StartZ=0 EndX=-112.85 EndY=-32 EndZ=0
    g6: LineSegment StartX=-112.85 StartY=-32 StartZ=0 EndX=-118.75 EndY=-32 EndZ=0
    g7: Circle CenterX=-111.75 CenterY=-25 CenterZ=0 NormalX=0 NormalY=0 NormalZ=1 AngleXU=0 Radius=3.5
    g8: LineSegment StartX=-118.75 StartY=-62 StartZ=0 EndX=-104.75 EndY=-62 EndZ=0
    g9: LineSegment StartX=-104.75 StartY=-76 StartZ=0 EndX=-110.65 EndY=-76 EndZ=0
    g10: LineSegment StartX=-110.65 StartY=-76 StartZ=0 EndX=-110.65 EndY=-74 EndZ=0
    g11: LineSegment StartX=-110.65 StartY=-74 StartZ=0 EndX=-112.85 EndY=-74 EndZ=0
    g12: LineSegment StartX=-112.85 StartY=-74 StartZ=0 EndX=-112.85 EndY=-76 EndZ=0
    g13: LineSegment StartX=-112.85 StartY=-76 StartZ=0 EndX=-118.75 EndY=-76 EndZ=0
    g14: Circle CenterX=-111.75 CenterY=-69 CenterZ=0 NormalX=0 NormalY=0 NormalZ=1 AngleXU=0 Radius=3.5
    g15: LineSegment StartX=104.75 StartY=-18 StartZ=0 EndX=118.75 EndY=-18 EndZ=0
    g16: LineSegment StartX=118.75 StartY=-32 StartZ=0 EndX=112.85 EndY=-32 EndZ=0
    g17: LineSegment StartX=112.85 StartY=-32 StartZ=0 EndX=112.85 EndY=-30 EndZ=0
    g18: LineSegment StartX=112.85 StartY=-30 StartZ=0 EndX=110.65 EndY=-30 EndZ=0
    g19: LineSegment StartX=110.65 StartY=-30 StartZ=0 EndX=110.65 EndY=-32 EndZ=0
    g20: LineSegment StartX=110.65 StartY=-32 StartZ=0 EndX=104.75 EndY=-32 EndZ=0
    g21: LineSegment StartX=104.75 StartY=-32 StartZ=0 EndX=104.75 EndY=-18 EndZ=0
    g22: Circle CenterX=111.75 CenterY=-25 CenterZ=0 NormalX=0 NormalY=0 NormalZ=1 AngleXU=0 Radius=3.5
    g23: LineSegment StartX=104.75 StartY=-62 StartZ=0 EndX=118.75 EndY=-62 EndZ=0
    g24: LineSegment StartX=118.75 StartY=-76 StartZ=0 EndX=112.85 EndY=-76 EndZ=0
    g25: LineSegment StartX=112.85 StartY=-76 StartZ=0 EndX=112.85 EndY=-74 EndZ=0
    g26: LineSegment StartX=112.85 StartY=-74 StartZ=0 EndX=110.65 EndY=-74 EndZ=0
    g27: LineSegment StartX=110.65 StartY=-74 StartZ=0 EndX=110.65 EndY=-76 EndZ=0
    g28: LineSegment StartX=110.65 StartY=-76 StartZ=0 EndX=104.75 EndY=-76 EndZ=0
    g29: LineSegment StartX=104.75 StartY=-76 StartZ=0 EndX=104.75 EndY=-62 EndZ=0
    g30: Circle CenterX=111.75 CenterY=-69 CenterZ=0 NormalX=0 NormalY=0 NormalZ=1 AngleXU=0 Radius=3.5
    g31: LineSegment StartX=-104.75 StartY=-62 StartZ=0 EndX=-104.75 EndY=-76 EndZ=0
    g32: LineSegment StartX=-118.75 StartY=-18 StartZ=0 EndX=-118.75 EndY=-23.9 EndZ=0
    g33: LineSegment StartX=-118.75 StartY=-23.9 StartZ=0 EndX=-116.75 EndY=-23.9 EndZ=0
    g34: LineSegment StartX=-116.75 StartY=-23.9 StartZ=0 EndX=-116.75 EndY=-26.1 EndZ=0
    g35: LineSegment StartX=-116.75 StartY=-26.1 StartZ=0 EndX=-118.75 EndY=-26.1 EndZ=0
    g36: LineSegment StartX=-118.75 StartY=-26.1 StartZ=0 EndX=-118.75 EndY=-32 EndZ=0
    g37: LineSegment StartX=-118.75 StartY=-76 StartZ=0 EndX=-118.75 EndY=-70.1 EndZ=0
    g38: LineSegment StartX=-118.75 StartY=-70.1 StartZ=0 EndX=-116.75 EndY=-70.1 EndZ=0
    g39: LineSegment StartX=-116.75 StartY=-70.1 StartZ=0 EndX=-116.75 EndY=-67.9 EndZ=0
    g40: LineSegment StartX=-116.75 StartY=-67.9 StartZ=0 EndX=-118.75 EndY=-67.9 EndZ=0
    g41: LineSegment StartX=-118.75 StartY=-67.9 StartZ=0 EndX=-118.75 EndY=-62 EndZ=0
    g42: LineSegment StartX=118.75 StartY=-76 StartZ=0 EndX=118.75 EndY=-70.1 EndZ=0
    g43: LineSegment StartX=118.75 StartY=-70.1 StartZ=0 EndX=116.75 EndY=-70.1 EndZ=0
    g44: LineSegment StartX=116.75 StartY=-70.1 StartZ=0 EndX=116.75 EndY=-67.9 EndZ=0
    g45: LineSegment StartX=116.75 StartY=-67.9 StartZ=0 EndX=118.75 EndY=-67.9 EndZ=0
    g46: LineSegment StartX=118.75 StartY=-67.9 StartZ=0 EndX=118.75 EndY=-62 EndZ=0
    g47: LineSegment StartX=118.75 StartY=-32 StartZ=0 EndX=118.75 EndY=-26.1 EndZ=0
    g48: LineSegment StartX=118.75 StartY=-26.1 StartZ=0 EndX=116.75 EndY=-26.1 EndZ=0
    g49: LineSegment StartX=116.75 StartY=-26.1 StartZ=0 EndX=116.75 EndY=-23.9 EndZ=0
    g50: LineSegment StartX=116.75 StartY=-23.9 StartZ=0 EndX=118.75 EndY=-23.9 EndZ=0
    g51: LineSegment StartX=118.75 StartY=-23.9 StartZ=0 EndX=118.75 EndY=-18 EndZ=0
  constraints (148):
    c: Horizontal(g0)
    c: Coincident(g0,g1)
    c: Vertical(g1)
    c: Coincident(g1,g2)
    c: Horizontal(g2)
    c: Coincident(g2,g3)
    c: Coincident(g3,g4)
    c: Coincident(g4,g5)
    c: Vertical(g5)
    c: Coincident(g5,g6)
    c: Horizontal(g6)
    c: Horizontal(g4)
    c: Vertical(g3)
    c: Symmetric(g6,g0,g7)
    c: Horizontal(g5,g2)
    c: DistanceX(g4,g4) = 2.2
    c: DistanceX(g0,g0) = 14
    c: DistanceY(g6,g0) = 14
    c: DistanceY(g3,g3) = 2
    c: Equal(g6,g2)
    c: Horizontal(g8)
    c: Horizontal(g9)
    c: Coincident(g9,g10)
    c: Coincident(g10,g11)
    c: Coincident(g11,g12)
    c: Vertical(g12)
    c: Coincident(g12,g13)
    c: Horizontal(g13)
    c: Horizontal(g11)
    c: Vertical(g10)
    c: Symmetric(g13,g8,g14)
    c: Horizontal(g12,g9)
    c: Equal(g4,g11) = 2.2
    c: Equal(g0,g8) = 14
    c: Equal(g3,g10) = 2
    c: Equal(g13,g9)
    c: Horizontal(g15)
    c: Horizontal(g16)
    c: Coincident(g16,g17)
    c: Coincident(g17,g18)
    c: Coincident(g18,g19)
    c: Vertical(g19)
    c: Coincident(g19,g20)
    c: Coincident(g20,g21)
    c: Coincident(g21,g15)
    c: Vertical(g21)
    c: Horizontal(g20)
    c: Horizontal(g18)
    c: Vertical(g17)
    c: Symmetric(g20,g15,g22)
    c: Horizontal(g19,g16)
    c: Equal(g4,g18) = 2.2
    c: Equal(g0,g15) = 14
    c: Equal(g3,g17) = 2
    c: Equal(g20,g16)
    c: Horizontal(g23)
    c: Horizontal(g24)
    c: Coincident(g24,g25)
    c: Coincident(g25,g26)
    c: Coincident(g26,g27)
    c: Vertical(g27)
    c: Coincident(g27,g28)
    c: Coincident(g28,g29)
    c: Coincident(g29,g23)
    c: Vertical(g29)
    c: Horizontal(g28)
    c: Horizontal(g26)
    c: Vertical(g25)
    c: Symmetric(g28,g23,g30)
    c: Horizontal(g27,g24)
    c: Equal(g4,g26) = 2.2
    c: Equal(g0,g23) = 14
    c: Equal(g3,g25) = 2
    c: Equal(g28,g24)
    c: Equal(g7,g22)
    c: Equal(g22,g30)
    c: Coincident(g31,g8)
    c: Coincident(g31,g9)
    c: Vertical(g31)
    c: Coincident(g0,g32)
    c: Vertical(g32)
    c: Coincident(g32,g33)
    c: Horizontal(g33)
    c: Coincident(g33,g34)
    c: Vertical(g34)
    c: Coincident(g34,g35)
    c: Horizontal(g35)
    c: Coincident(g35,g36)
    c: Coincident(g36,g6)
    c: Vertical(g36)
    c: Coincident(g13,g37)
    c: Vertical(g37)
    c: Coincident(g37,g38)
    c: Horizontal(g38)
    c: Coincident(g38,g39)
    c: Vertical(g39)
    c: Coincident(g39,g40)
    c: Horizontal(g40)
    c: Coincident(g40,g41)
    c: Coincident(g41,g8)
    c: Vertical(g41)
    c: Coincident(g24,g42)
    c: Vertical(g42)
    c: Coincident(g42,g43)
    c: Horizontal(g43)
    c: Coincident(g43,g44)
    c: Vertical(g44)
    c: Coincident(g44,g45)
    c: Horizontal(g45)
    c: Coincident(g45,g46)
    c: Coincident(g46,g23)
    c: Vertical(g46)
    c: Coincident(g16,g47)
    c: Vertical(g47)
    c: Coincident(g47,g48)
    c: Horizontal(g48)
    c: Coincident(g48,g49)
    c: Vertical(g49)
    c: Coincident(g49,g50)
    c: Horizontal(g50)
    c: Coincident(g50,g51)
    c: Coincident(g51,g15)
    c: Vertical(g51)
    c: Equal(g51,g47)
    c: Equal(g18,g49)
    c: Equal(g17,g48)
    c: Vertical(g47,g50)
    c: Equal(g46,g42)
    c: Equal(g44,g26)
    c: Equal(g25,g43)
    c: Equal(g32,g36)
    c: Equal(g34,g4)
    c: Equal(g35,g5)
    c: Equal(g11,g39)
    c: Equal(g38,g12)
    c: Equal(g37,g41)
    c: Vertical(g40,g37)
    c: Vertical(g32,g35)
    c: Vertical(g45,g42)
    c: Equal(g1,g31)
    c: Equal(g1,g21)
    c: Equal(g1,g29)
    c: Equal(g7,g-4)
    c: Coincident(g-4,g7)
    c: Coincident(g-5,g14)
    c: Equal(g14,g7)
    c: Coincident(g30,g-6)
    c: Coincident(g22,g-7)
FEATURE [PartDesign::Pad] Pad003  label="Knob Index Pads"
  BaseFeature = -> Pocket003
  Direction = (7e-16,-7e-16,-1)
  Length = 1
  Length2 = 10
  Profile = -> Sketch008
  ReferenceAxis = -> Sketch008 [N_Axis]
  Type = 0
FEATURE [Sketcher::SketchObject] Sketch009
  ExternalGeometry = -> [Pad003]
  FullyConstrained = true
  MapMode = 5
  Placement = pos=(-1.35e-14,2.11e-14,48.05) rot=(1,0,0;3.14159rad)
  Support = -> [Pad003]
  sketch-geometry (8):
    g0: LineSegment StartX=129.05 StartY=-95.145 StartZ=0 EndX=129.05 EndY=-99.05 EndZ=0
    g1: LineSegment StartX=129.05 StartY=-99.05 StartZ=0 EndX=147.05 EndY=-99.05 EndZ=0
    g2: LineSegment StartX=147.05 StartY=-99.05 StartZ=0 EndX=147.05 EndY=-78.7531 EndZ=0
    g3: LineSegment StartX=-129.05 StartY=-99.05 StartZ=0 EndX=-129.05 EndY=-95.145 EndZ=0
    g4: LineSegment StartX=-129.05 StartY=-99.05 StartZ=0 EndX=-147.05 EndY=-99.05 EndZ=0
    g5: LineSegment StartX=-147.05 StartY=-99.05 StartZ=0 EndX=-147.05 EndY=-78.7531 EndZ=0
    g6: ArcOfCircle CenterX=-150 CenterY=-100.071 CenterZ=0 NormalX=0 NormalY=0 NormalZ=1 AngleXU=0 Radius=21.5214 StartAngle=0.230954 EndAngle=1.43329
    g7: ArcOfCircle CenterX=150 CenterY=-100.071 CenterZ=0 NormalX=0 NormalY=0 NormalZ=1 AngleXU=0 Radius=21.5214 StartAngle=1.7083 EndAngle=2.91064
  constraints (19):
    c: Coincident(g0,g1)
    c: Coincident(g1,g2)
    c: Coincident(g3,g4)
    c: Coincident(g4,g5)
    c: Coincident(g6,g3)
    c: Coincident(g6,g5)
    c: Horizontal(g1)
    c: Vertical(g2)
    c: Coincident(g3,g-4)
    c: Coincident(g4,g-3)
    c: Coincident(g3,g-5)
    c: Coincident(g5,g-5)
    c: Equal(g6,g-5)
    c: Coincident(g0,g-8)
    c: Coincident(g0,g-7)
    c: Coincident(g7,g0)
    c: Coincident(g7,g2)
    c: Coincident(g2,g-7)
    c: Equal(g7,g-7)
FEATURE [PartDesign::Pad] Pad004  label="Edge Cutout Gap Closing"
  BaseFeature = -> Pad003
  Direction = (3e-16,-4e-16,-1)
  Length = 1
  Length2 = 10
  Midplane = true
  Profile = -> Sketch009
  ReferenceAxis = -> Sketch009 [N_Axis]
  Type = 0
FEATURE [PartDesign::Plane] DatumPlane  label="LeftSupport DatumPlane"
  AttachmentOffset = pos=(0,0,-63) rot=(0,0,1;0rad)
  Length = 146.649
  MapMode = 5
  Placement = pos=(-63,1.4e-14,-1.4e-14) rot=(0.57735,0.57735,0.57735;2.0944rad)
  ResizeMode = 0
  Support = -> [YZ_Plane038]
  Width = 95.6489
FEATURE [PartDesign::Plane] DatumPlane001  label="RightSupport DatumPlane"
  AttachmentOffset = pos=(0,0,62) rot=(0,0,1;0rad)
  Length = 146.649
  MapMode = 5
  Placement = pos=(62,-1.38e-14,1.38e-14) rot=(0.57735,0.57735,0.57735;2.0944rad)
  ResizeMode = 0
  Support = -> [YZ_Plane038]
  Width = 95.6489
FEATURE [Sketcher::SketchObject] Sketch010
  ExternalGeometry = -> [Pad004]
  FullyConstrained = true
  MapMode = 5
  Placement = pos=(-63,1.4e-14,-1.4e-14) rot=(0.57735,0.57735,0.57735;2.0944rad)
  Support = -> [DatumPlane]
  sketch-geometry (12):
    g0: LineSegment StartX=-4 StartY=48.05 StartZ=0 EndX=-4 EndY=44.85 EndZ=0
    g1: LineSegment StartX=-4 StartY=44.85 StartZ=0 EndX=-1.1 EndY=41.95 EndZ=0
    g2: LineSegment StartX=-1.1 StartY=41.95 StartZ=0 EndX=96.15 EndY=41.95 EndZ=0
    g3: LineSegment StartX=96.15 StartY=41.95 StartZ=0 EndX=99.05 EndY=44.85 EndZ=0
    g4: LineSegment StartX=96.05 StartY=39.15 StartZ=0 EndX=-5.05 EndY=39.15 EndZ=0
    g5: LineSegment StartX=-8.05 StartY=48.05 StartZ=0 EndX=-4 EndY=48.05 EndZ=0
    g6: LineSegment StartX=-8.05 StartY=48.05 StartZ=0 EndX=-8.05 EndY=40 EndZ=0
    g7: LineSegment StartX=-8.05 StartY=40 StartZ=0 EndX=-5.05 EndY=40 EndZ=0
    g8: LineSegment StartX=-5.05 StartY=40 StartZ=0 EndX=-5.05 EndY=39.15 EndZ=0
    g9: LineSegment StartX=99.05 StartY=44.85 StartZ=0 EndX=99.05 EndY=40 EndZ=0
    g10: LineSegment StartX=99.05 StartY=40 StartZ=0 EndX=96.05 EndY=40 EndZ=0
    g11: LineSegment StartX=96.05 StartY=40 StartZ=0 EndX=96.05 EndY=39.15 EndZ=0
  constraints (33):
    c: Vertical(g8)
    c: Horizontal(g7)
    c: Horizontal(g4)
    c: Horizontal(g2)
    c: Vertical(g0)
    c: Vertical(g11)
    c: Vertical(g9)
    c: Horizontal(g10)
    c: Coincident(g0,g5)
    c: Coincident(g5,g6)
    c: Coincident(g7,g6)
    c: Coincident(g7,g8)
    c: Coincident(g4,g8)
    c: Coincident(g0,g1)
    c: Coincident(g2,g1)
    c: DistanceY(g0,g0) = 3.2
    c: DistanceX(g7,g7) = 3
    c: DistanceY(g1,g0) = 2.9
    c: Angle(g1,g0) = 2.35619
    c: DistanceY(g4,g1) = 2.8
    c: Coincident(g4,g11)
    c: Coincident(g10,g11)
    c: Coincident(g10,g9)
    c: Coincident(g9,g3)
    c: Coincident(g2,g3)
    c: DistanceX(g10,g10) = 3
    c: Angle(g3,g9) = 0.785398
    c: Horizontal(g0,g3)
    c: Vertical(g6)
    c: Horizontal(g5)
    c: Coincident(g6,g-5)
    c: Coincident(g0,g-4)
    c: Coincident(g9,g-3)
FEATURE [PartDesign::Pad] Pad006  label="LeftSupport"
  BaseFeature = -> Pad004
  Direction = (1,-1e-16,1e-16)
  Length = 20
  Length2 = 10
  Midplane = true
  Profile = -> Sketch010
  ReferenceAxis = -> Sketch010 [N_Axis]
  Type = 0
FEATURE [Sketcher::SketchObject] Sketch012
  ExternalGeometry = -> [Pad004]
  FullyConstrained = true
  MapMode = 5
  Placement = pos=(62,-1.38e-14,1.38e-14) rot=(0.57735,0.57735,0.57735;2.0944rad)
  Support = -> [DatumPlane001]
  expr: Constraints[15] = Sketch010.Constraints[15]
  expr: Constraints[16] = Sketch010.Constraints[16]
  expr: Constraints[17] = Sketch010.Constraints[17]
  expr: Constraints[18] = Sketch010.Constraints[18]
  expr: Constraints[19] = Sketch010.Constraints[19]
  expr: Constraints[25] = Sketch010.Constraints[25]
  expr: Constraints[26] = Sketch010.Constraints[26]
  sketch-geometry (12):
    g0: LineSegment StartX=-4 StartY=48.05 StartZ=0 EndX=-4 EndY=44.85 EndZ=0
    g1: LineSegment StartX=-4 StartY=44.85 StartZ=0 EndX=-1.1 EndY=41.95 EndZ=0
    g2: LineSegment StartX=-1.1 StartY=41.95 StartZ=0 EndX=96.15 EndY=41.95 EndZ=0
    g3: LineSegment StartX=96.15 StartY=41.95 StartZ=0 EndX=99.05 EndY=44.85 EndZ=0
    g4: LineSegment StartX=96.05 StartY=39.15 StartZ=0 EndX=-5.05 EndY=39.15 EndZ=0
    g5: LineSegment StartX=-8.05 StartY=48.05 StartZ=0 EndX=-4 EndY=48.05 EndZ=0
    g6: LineSegment StartX=-8.05 StartY=48.05 StartZ=0 EndX=-8.05 EndY=40 EndZ=0
    g7: LineSegment StartX=-8.05 StartY=40 StartZ=0 EndX=-5.05 EndY=40 EndZ=0
    g8: LineSegment StartX=-5.05 StartY=40 StartZ=0 EndX=-5.05 EndY=39.15 EndZ=0
    g9: LineSegment StartX=99.05 StartY=44.85 StartZ=0 EndX=99.05 EndY=40 EndZ=0
    g10: LineSegment StartX=99.05 StartY=40 StartZ=0 EndX=96.05 EndY=40 EndZ=0
    g11: LineSegment StartX=96.05 StartY=40 StartZ=0 EndX=96.05 EndY=39.15 EndZ=0
  constraints (33):
    c: Vertical(g8)
    c: Horizontal(g7)
    c: Horizontal(g4)
    c: Horizontal(g2)
    c: Vertical(g0)
    c: Vertical(g11)
    c: Vertical(g9)
    c: Horizontal(g10)
    c: Coincident(g0,g5)
    c: Coincident(g5,g6)
    c: Coincident(g7,g6)
    c: Coincident(g7,g8)
    c: Coincident(g4,g8)
    c: Coincident(g0,g1)
    c: Coincident(g2,g1)
    c: DistanceY(g0,g0) = 3.2
    c: DistanceX(g7,g7) = 3
    c: DistanceY(g1,g0) = 2.9
    c: Angle(g1,g0) = 2.35619
    c: DistanceY(g4,g1) = 2.8
    c: Coincident(g4,g11)
    c: Coincident(g10,g11)
    c: Coincident(g10,g9)
    c: Coincident(g9,g3)
    c: Coincident(g2,g3)
    c: DistanceX(g10,g10) = 3
    c: Angle(g3,g9) = 0.785398
    c: Horizontal(g0,g3)
    c: Vertical(g6)
    c: Horizontal(g5)
    c: Coincident(g6,g-4)
    c: Coincident(g0,g-3)
    c: Coincident(g9,g-5)
FEATURE [PartDesign::Pad] Pad007  label="RightSupport"
  BaseFeature = -> Pad006
  Direction = (1,-1e-16,1e-16)
  Length = 20
  Length2 = 10
  Midplane = true
  Profile = -> Sketch012
  ReferenceAxis = -> Sketch012 [N_Axis]
  Type = 0
FEATURE [PartDesign::Plane] DatumPlane003  label="Screwpost DatumPlane"
  AttachmentOffset = pos=(0,0,32) rot=(0,0,1;0rad)
  Length = 339.038
  MapMode = 5
  Placement = pos=(0,0,32) rot=(0,0,1;0rad)
  ResizeMode = 0
  Support = -> [XY_Plane038]
  Width = 166.038
FEATURE [PartDesign::Body] Body006  label="Top Cover"
  Group = -> [Sketch005,Pad002,Sketch006,Pocket002,Thickness001,Sketch007,Pocket003,Sketch008,Pad003,Sketch009,Pad004,DatumPlane,DatumPlane001,Sketch010,Pad006,Sketch012,Pad007,Sketch032,Pocket010,DatumPlane003,Sketch033,Sketch034,Pad013,Sketch035,Pad014,Sketch036,Pocket011,Chamfer]
  Origin = -> Origin038
  Tip = -> Chamfer
FEATURE [Sketcher::SketchObject] Sketch032
  ExternalGeometry = -> [Pad007]
  FullyConstrained = true
  MapMode = 5
  Placement = pos=(-4.3e-15,4.3e-15,39.15) rot=(1,0,0;3.14159rad)
  Support = -> [Cut]
  sketch-geometry (4):
    g0: Circle CenterX=-64 CenterY=-11.65 CenterZ=0 NormalX=0 NormalY=0 NormalZ=1 AngleXU=0 Radius=1.6
    g1: Circle CenterX=-64 CenterY=-77.35 CenterZ=0 NormalX=0 NormalY=0 NormalZ=1 AngleXU=0 Radius=1.6
    g2: Circle CenterX=62.5 CenterY=-11.65 CenterZ=0 NormalX=0 NormalY=0 NormalZ=1 AngleXU=0 Radius=1.6
    g3: Circle CenterX=62.5 CenterY=-77.35 CenterZ=0 NormalX=0 NormalY=0 NormalZ=1 AngleXU=0 Radius=1.6
  constraints (12):
    c: Equal(g0,g1)
    c: Equal(g1,g3)
    c: Equal(g3,g2)
    c: Vertical(g3,g2)
    c: Diameter(g0) = 3.2
    c: DistanceY(g3,g2) = 65.7
    c: DistanceX(g0,g2) = 126.5
    c: Horizontal(g0,g2)
    c: Horizontal(g1,g3)
    c: Vertical(g1,g0)
    c: DistanceX(g0,g-1) = 64
    c: DistanceY(g0,g-3) = 15.65
FEATURE [PartDesign::Pocket] Pocket010  label="Display Screwholes"
  BaseFeature = -> Pad007
  Direction = (-1e-16,1e-16,1)
  Length = 5
  Length2 = 5
  Profile = -> Sketch032
  ReferenceAxis = -> Sketch032 [N_Axis]
  Type = 1
FEATURE [Sketcher::SketchObject] Sketch033  label="Screwposts Top Sketch"
  ExternalGeometry = -> [Pocket010]
  FullyConstrained = true
  MapMode = 5
  Placement = pos=(0,0,32) rot=(0,1,0;3.14159rad)
  Support = -> [DatumPlane003]
  sketch-geometry (6):
    g0: Circle CenterX=-136 CenterY=10 CenterZ=0 NormalX=0 NormalY=0 NormalZ=1 AngleXU=0 Radius=5.5
    g1: Circle CenterX=136 CenterY=10 CenterZ=0 NormalX=0 NormalY=0 NormalZ=1 AngleXU=0 Radius=5.5
    g2: Circle CenterX=63 CenterY=64 CenterZ=0 NormalX=0 NormalY=0 NormalZ=1 AngleXU=0 Radius=5.5
    g3: Circle CenterX=-60 CenterY=22 CenterZ=0 NormalX=0 NormalY=0 NormalZ=1 AngleXU=0 Radius=5.5
    g4: Circle CenterX=-136 CenterY=55 CenterZ=0 NormalX=0 NormalY=0 NormalZ=1 AngleXU=0 Radius=5.5
    g5: Circle CenterX=136 CenterY=55 CenterZ=0 NormalX=0 NormalY=0 NormalZ=1 AngleXU=0 Radius=5.5
  constraints (19):
    c: Symmetric(g0,g1,g-2)
    c: Equal(g0,g3)
    c: Equal(g3,g2)
    c: Equal(g2,g1)
    c: Diameter(g0) = 11
    c: DistanceY(g-1,g0) = 10
    c: DistanceX(g0,g-1) = 136
    c: DistanceX(g3,g-1) = 60
    c: DistanceX(g-1,g2) = 63
    c: DistanceY(g2,g-3) = 38
    c: DistanceY(g-1,g2) = 64
    c: DistanceY(g-1,g3) = 22
    c: DistanceY(g3,g-3) = 80
    c: Equal(g4,g5)
    c: Equal(g5,g1)
    c: Vertical(g0,g4)
    c: Vertical(g5,g1)
    c: DistanceY(g0,g4) = 45
    c: Horizontal(g5,g4)
FEATURE [Sketcher::SketchObject] Sketch034
  ExternalGeometry = -> [Sketch033]
  FullyConstrained = true
  MapMode = 5
  Placement = pos=(0,0,32) rot=(0,0,1;0rad)
  Support = -> [DatumPlane003]
  sketch-geometry (4):
    g0: Circle CenterX=-136 CenterY=10 CenterZ=0 NormalX=0 NormalY=0 NormalZ=1 AngleXU=0 Radius=5.5
    g1: Circle CenterX=136 CenterY=10 CenterZ=0 NormalX=0 NormalY=0 NormalZ=1 AngleXU=0 Radius=5.5
    g2: Circle CenterX=-136 CenterY=55 CenterZ=0 NormalX=0 NormalY=0 NormalZ=1 AngleXU=0 Radius=5.5
    g3: Circle CenterX=136 CenterY=55 CenterZ=0 NormalX=0 NormalY=0 NormalZ=1 AngleXU=0 Radius=5.5
  constraints (8):
    c: Equal(g2,g-5)
    c: Equal(g0,g-3)
    c: Equal(g1,g-4)
    c: Equal(g3,g-6)
    c: Coincident(g3,g-6)
    c: Coincident(g1,g-4)
    c: Coincident(g-3,g0)
    c: Coincident(g-5,g2)
FEATURE [PartDesign::Pad] Pad013  label="Outer Screwposts"
  BaseFeature = -> Pocket010
  Direction = (0,0,1)
  Length = 13
  Length2 = 10
  Profile = -> Sketch034
  ReferenceAxis = -> Sketch034 [N_Axis]
  Type = 3
  UpToFace = -> Pocket010 [Face25]
FEATURE [Sketcher::SketchObject] Sketch035
  ExternalGeometry = -> [Sketch033]
  FullyConstrained = true
  MapMode = 5
  Placement = pos=(0,0,32) rot=(0,0,1;0rad)
  Support = -> [DatumPlane003]
  sketch-geometry (2):
    g0: Circle CenterX=-63 CenterY=64 CenterZ=0 NormalX=0 NormalY=0 NormalZ=1 AngleXU=0 Radius=5.5
    g1: Circle CenterX=60 CenterY=22 CenterZ=0 NormalX=0 NormalY=0 NormalZ=1 AngleXU=0 Radius=5.5
  constraints (4):
    c: Coincident(g0,g-3)
    c: Coincident(g1,g-4)
    c: Equal(g0,g-3)
    c: Equal(g1,g-4)
FEATURE [PartDesign::Pad] Pad014  label="Inner Screwposts"
  BaseFeature = -> Pad013
  Direction = (0,0,1)
  Length = 4.2
  Length2 = 10
  Profile = -> Sketch035
  ReferenceAxis = -> Sketch035 [N_Axis]
  Type = 3
  UpToFace = -> Pad013 [Face124]
FEATURE [Sketcher::SketchObject] Sketch036
  ExternalGeometry = -> [Sketch033]
  FullyConstrained = true
  MapMode = 5
  Placement = pos=(0,0,32) rot=(0,0,1;0rad)
  Support = -> [DatumPlane003]
  sketch-geometry (6):
    g0: Circle CenterX=-136 CenterY=10 CenterZ=0 NormalX=0 NormalY=0 NormalZ=1 AngleXU=0 Radius=2.8
    g1: Circle CenterX=136 CenterY=10 CenterZ=0 NormalX=0 NormalY=0 NormalZ=1 AngleXU=0 Radius=2.8
    g2: Circle CenterX=-63 CenterY=64 CenterZ=0 NormalX=0 NormalY=0 NormalZ=1 AngleXU=0 Radius=2.8
    g3: Circle CenterX=60 CenterY=22 CenterZ=0 NormalX=0 NormalY=0 NormalZ=1 AngleXU=0 Radius=2.8
    g4: Circle CenterX=-136 CenterY=55 CenterZ=0 NormalX=0 NormalY=0 NormalZ=1 AngleXU=0 Radius=2.8
    g5: Circle CenterX=136 CenterY=55 CenterZ=0 NormalX=0 NormalY=0 NormalZ=1 AngleXU=0 Radius=2.8
  constraints (12):
    c: Coincident(g0,g-3)
    c: Coincident(g1,g-4)
    c: Equal(g0,g1)
    c: Diameter(g0) = 5.6
    c: Coincident(g2,g-5)
    c: Coincident(g3,g-6)
    c: Equal(g2,g3)
    c: Equal(g3,g0)
    c: Coincident(g4,g-7)
    c: Coincident(g5,g-8)
    c: Equal(g5,g4)
    c: Equal(g4,g2)
FEATURE [PartDesign::Pocket] Pocket011  label="M4 Insert Pocket"
  BaseFeature = -> Pad014
  Direction = (0,0,-1)
  Length = 9
  Length2 = 5
  Profile = -> Sketch036
  ReferenceAxis = -> Sketch036 [N_Axis]
  Reversed = true
  Type = 0
FEATURE [PartDesign::Chamfer] Chamfer
  Angle = 55
  Base = -> Pocket011 [Edge1,Edge2,Edge4,Edge3]
  BaseFeature = -> Pocket011
  ChamferType = 2
  FlipDirection = false
  Size = 0.3
  Size2 = 1
  SupportTransform = false
  UseAllEdges = false
COMPONENT P3 — recipe-attached ("SplitPlane", modeled in this document).
Construction recipe (the document's own serialized feature program — sketch geometry with constraints, then the solid features built on it; lengths are millimeters unless a unit is written):

FEATURE [Sketcher::SketchObject] Sketch015
  FullyConstrained = true
  MapMode = 5
  Placement = pos=(0,0,0) rot=(0.57735,0.57735,0.57735;2.0944rad)
  Support = -> [YZ_Plane042]
  sketch-geometry (4):
    g0: LineSegment StartX=-25 StartY=70 StartZ=0 EndX=135 EndY=70 EndZ=0
    g1: LineSegment StartX=135 StartY=70 StartZ=0 EndX=135 EndY=-10 EndZ=0
    g2: LineSegment StartX=135 StartY=-10 StartZ=0 EndX=-25 EndY=-10 EndZ=0
    g3: LineSegment StartX=-25 StartY=-10 StartZ=0 EndX=-25 EndY=70 EndZ=0
  constraints (12):
    c: Coincident(g0,g1)
    c: Coincident(g1,g2)
    c: Coincident(g2,g3)
    c: Coincident(g3,g0)
    c: Horizontal(g0)
    c: Horizontal(g2)
    c: Vertical(g1)
    c: Vertical(g3)
    c: DistanceX(g0,g0) = 160
    c: DistanceX(g2,g-1) = 25
    c: DistanceY(g1,g1) = 80
    c: DistanceY(g2,g-1) = 10
FEATURE [PartDesign::Pad] Pad008
  Direction = (1,-2e-16,3e-16)
  Length = 0.1
  Length2 = 10
  Midplane = true
  Placement = pos=(0,0,0) rot=(0.57735,0.57735,0.57735;2.0944rad)
  Profile = -> Sketch015
  ReferenceAxis = -> Sketch015 [N_Axis]
  Type = 0
FEATURE [PartDesign::Body] Body010  label="SplitPlane"
  Group = -> [Sketch015,Pad008]
  Origin = -> Origin042
  Tip = -> Pad008
COMPONENT P4 — recipe-attached ("TopLeft Cover Body", modeled in this document).
Construction recipe (the document's own serialized feature program — sketch geometry with constraints, then the solid features built on it; lengths are millimeters unless a unit is written):

FEATURE [PartDesign::Body] Body011  label="TopLeft Cover Body"
  Group = -> [Clone005]
  Origin = -> Origin043
  Tip = -> Clone005
FEATURE [PartDesign::FeatureBase] Clone005
  BaseFeature = -> Slice_child0
COMPONENT P5 — recipe-attached ("TopRight Cover Body", modeled in this document).
Construction recipe (the document's own serialized feature program — sketch geometry with constraints, then the solid features built on it; lengths are millimeters unless a unit is written):

FEATURE [PartDesign::Body] Body012  label="TopRight Cover Body"
  Group = -> [Clone006]
  Origin = -> Origin044
  Tip = -> Clone006
FEATURE [PartDesign::FeatureBase] Clone006
  BaseFeature = -> Slice_child3
COMPONENT P6 — recipe-attached ("TopCover Cutout Clone", modeled in this document).
Construction recipe (the document's own serialized feature program — sketch geometry with constraints, then the solid features built on it; lengths are millimeters unless a unit is written):

FEATURE [PartDesign::Body] Body013  label="TopCover Cutout Clone"
  Group = -> [Clone007]
  Origin = -> Origin045
  Tip = -> Clone007
FEATURE [PartDesign::FeatureBase] Clone007
  BaseFeature = -> Cut
COMPONENT P7 — recipe-attached ("BottomLeft Body", modeled in this document).
Construction recipe (the document's own serialized feature program — sketch geometry with constraints, then the solid features built on it; lengths are millimeters unless a unit is written):

FEATURE [PartDesign::Body] Body014  label="BottomLeft Body"
  Group = -> [Clone008]
  Origin = -> Origin046
  Tip = -> Clone008
FEATURE [PartDesign::FeatureBase] Clone008
  BaseFeature = -> Slice001_child0
COMPONENT P8 — recipe-attached ("BottomRight Body", modeled in this document).
Construction recipe (the document's own serialized feature program — sketch geometry with constraints, then the solid features built on it; lengths are millimeters unless a unit is written):

FEATURE [PartDesign::Body] Body015  label="BottomRight Body"
  Group = -> [Clone009]
  Origin = -> Origin047
  Tip = -> Clone009
FEATURE [PartDesign::FeatureBase] Clone009
  BaseFeature = -> Slice001_child2
COMPONENT P9 — recipe-attached ("AssemblyHelper", modeled in this document).
Construction recipe (the document's own serialized feature program — sketch geometry with constraints, then the solid features built on it; lengths are millimeters unless a unit is written):

FEATURE [PartDesign::Body] Body016  label="AssemblyHelper"
  Group = -> [ShapeBinder,Sketch039,Pad016]
  Origin = -> Origin048
  Tip = -> Pad016
FEATURE [PartDesign::ShapeBinder] ShapeBinder
  Support = -> [Clone008]
  TraceSupport = false
FEATURE [Sketcher::SketchObject] Sketch039
  ExternalGeometry = -> [ShapeBinder]
  FullyConstrained = true
  MapMode = 5
  Placement = pos=(0,0,0) rot=(0.57735,0.57735,0.57735;2.0944rad)
  Support = -> [YZ_Plane048]
  sketch-geometry (13):
    g0: LineSegment StartX=102 StartY=32.3995 StartZ=0 EndX=102 EndY=-7.82e-14 EndZ=0
    g1: LineSegment StartX=102 StartY=-7.82e-14 StartZ=0 EndX=1.847e-13 EndY=-8.17e-14 EndZ=0
    g2: LineSegment StartX=1.847e-13 StartY=-8.17e-14 StartZ=0 EndX=1.964e-13 EndY=14.5 EndZ=0
    g3: LineSegment StartX=1.964e-13 StartY=14.5 StartZ=0 EndX=-8.94975 EndY=23.4497 EndZ=0
    g4: ArcOfCircle CenterX=-4 CenterY=28.3995 CenterZ=0 NormalX=0 NormalY=0 NormalZ=1 AngleXU=0 Radius=7 StartAngle=3.14159 EndAngle=3.92699
    g5: LineSegment StartX=-11 StartY=28.3995 StartZ=0 EndX=-11 EndY=32.3995 EndZ=0
    g6: LineSegment StartX=-11 StartY=32.3995 StartZ=0 EndX=-13.5 EndY=32.3995 EndZ=0
    g7: LineSegment StartX=-13.5 StartY=32.3995 StartZ=0 EndX=-13.5 EndY=23.5 EndZ=0
    g8: LineSegment StartX=-13.5 StartY=23.5 StartZ=0 EndX=-2.5 EndY=12.5 EndZ=0
    g9: LineSegment StartX=-2.5 StartY=12.5 StartZ=0 EndX=-2.5 EndY=-2.5 EndZ=0
    g10: LineSegment StartX=-2.5 StartY=-2.5 StartZ=0 EndX=104.5 EndY=-2.5 EndZ=0
    g11: LineSegment StartX=104.5 StartY=-2.5 StartZ=0 EndX=104.5 EndY=32.3995 EndZ=0
    g12: LineSegment StartX=102 StartY=32.3995 StartZ=0 EndX=104.5 EndY=32.3995 EndZ=0
  constraints (34):
    c: Coincident(g0,g1)
    c: Coincident(g1,g2)
    c: Coincident(g2,g3)
    c: Tangent(g3,g4) = 1.5708
    c: Coincident(g4,g5)
    c: Coincident(g5,g6)
    c: Horizontal(g6)
    c: Coincident(g6,g7)
    c: Vertical(g7)
    c: Coincident(g7,g8)
    c: Coincident(g8,g9)
    c: Vertical(g9)
    c: Coincident(g9,g10)
    c: Horizontal(g10)
    c: Coincident(g10,g11)
    c: Vertical(g11)
    c: DistanceY(g10,g0) = 2.5
    c: DistanceX(g0,g11) = 2.5
    c: DistanceX(g9,g1) = 2.5
    c: DistanceX(g6,g6) = 2.5
    c: Parallel(g8,g3)
    c: DistanceY(g8,g2) = 2
    c: Coincident(g4,g-4)
    c: Coincident(g4,g-3)
    c: Vertical(g5)
    c: Coincident(g2,g-5)
    c: Coincident(g1,g-5)
    c: Coincident(g0,g-6)
    c: Vertical(g0)
    c: Coincident(g12,g0)
    c: Coincident(g12,g11)
    c: Horizontal(g12)
    c: Horizontal(g0,g5)
    c: DistanceY(g5,g5) = 4
FEATURE [PartDesign::Pad] Pad016
  Direction = (1,-2e-16,3e-16)
  Length = 25
  Length2 = 10
  Midplane = true
  Placement = pos=(0,0,0) rot=(1,1,1;2.0944rad)
  Profile = -> Sketch039
  ReferenceAxis = -> Sketch039 [N_Axis]
  Type = 0
COMPONENT P10 — recipe-attached ("BodyConnector", modeled in this document).
Construction recipe (the document's own serialized feature program — sketch geometry with constraints, then the solid features built on it; lengths are millimeters unless a unit is written):

FEATURE [PartDesign::Body] Body017  label="BodyConnector"
  Group = -> [ShapeBinder001,Sketch040,Pad017]
  Origin = -> Origin049
  Tip = -> Pad017
FEATURE [PartDesign::ShapeBinder] ShapeBinder001
  Support = -> [Body014]
  TraceSupport = false
FEATURE [Sketcher::SketchObject] Sketch040
  ExternalGeometry = -> [ShapeBinder001]
  FullyConstrained = true
  MapMode = 5
  Placement = pos=(0,0,0) rot=(0.57735,0.57735,0.57735;2.0944rad)
  Support = -> [YZ_Plane049]
  sketch-geometry (14):
    g0: LineSegment StartX=99 StartY=19 StartZ=0 EndX=99 EndY=3 EndZ=0
    g1: LineSegment StartX=99 StartY=3 StartZ=0 EndX=3 EndY=3 EndZ=0
    g2: LineSegment StartX=3 StartY=3 StartZ=0 EndX=3 EndY=15.7426 EndZ=0
    g3: LineSegment StartX=3 StartY=15.7426 StartZ=0 EndX=-6.82843 EndY=25.5711 EndZ=0
    g4: ArcOfCircle CenterX=-4 CenterY=28.3995 CenterZ=0 NormalX=0 NormalY=0 NormalZ=1 AngleXU=0 Radius=4 StartAngle=3.14159 EndAngle=3.92699
    g5: LineSegment StartX=-8 StartY=28.3995 StartZ=0 EndX=-8 EndY=34.3995 EndZ=0
    g6: LineSegment StartX=-8 StartY=34.3995 StartZ=0 EndX=-6.5 EndY=34.3995 EndZ=0
    g7: LineSegment StartX=-6.5 StartY=34.3995 StartZ=0 EndX=-6.5 EndY=28.3995 EndZ=0
    g8: ArcOfCircle CenterX=-4 CenterY=28.3995 CenterZ=0 NormalX=0 NormalY=0 NormalZ=1 AngleXU=0 Radius=2.5 StartAngle=3.14159 EndAngle=3.92699
    g9: LineSegment StartX=-5.76777 StartY=26.6317 StartZ=0 EndX=4.5 EndY=16.364 EndZ=0
    g10: LineSegment StartX=4.5 StartY=16.364 StartZ=0 EndX=4.5 EndY=4.5 EndZ=0
    g11: LineSegment StartX=4.5 StartY=4.5 StartZ=0 EndX=97.5 EndY=4.5 EndZ=0
    g12: LineSegment StartX=97.5 StartY=4.5 StartZ=0 EndX=97.5 EndY=19 EndZ=0
    g13: LineSegment StartX=97.5 StartY=19 StartZ=0 EndX=99 EndY=19 EndZ=0
  constraints (35):
    c: Coincident(g0,g1)
    c: Coincident(g1,g2)
    c: Coincident(g2,g3)
    c: Tangent(g3,g4) = 1.5708
    c: Coincident(g4,g5)
    c: Coincident(g5,g6)
    c: Horizontal(g6)
    c: Coincident(g6,g7)
    c: Vertical(g7)
    c: Tangent(g7,g8) = -1.5708
    c: Coincident(g9,g10)
    c: Vertical(g10)
    c: Coincident(g10,g11)
    c: Horizontal(g11)
    c: Coincident(g11,g12)
    c: Vertical(g12)
    c: Coincident(g12,g13)
    c: Coincident(g13,g0)
    c: Horizontal(g13)
    c: Parallel(g9,g3)
    c: Coincident(g4,g8)
    c: Tangent(g8,g9) = -1.5708
    c: DistanceX(g6,g6) = 1.5
    c: DistanceY(g5,g5) = 6
    c: DistanceX(g1,g10) = 1.5
    c: DistanceY(g1,g10) = 1.5
    c: DistanceX(g13,g13) = 1.5
    c: DistanceY(g0,g0) = 16
    c: Vertical(g0)
    c: Coincident(g0,g-4)
    c: Coincident(g1,g-4)
    c: Coincident(g2,g-3)
    c: Coincident(g3,g-3)
    c: Vertical(g5)
    c: Coincident(g4,g-5)
FEATURE [PartDesign::Pad] Pad017
  Direction = (1,-2e-16,3e-16)
  Length = 20
  Length2 = 10
  Midplane = true
  Placement = pos=(0,0,0) rot=(1,1,1;2.0944rad)
  Profile = -> Sketch040
  ReferenceAxis = -> Sketch040 [N_Axis]
  Type = 0
COMPONENT P11 — geometry summary ("MIDI Connector001"; no construction recipe available for this part):
  bounding box: 28.0 x 20.6 x 19.0 mm
  tessellated surface: 59,036 triangles
  volume: 2094 mm^3 (19% of its bounding box)
COMPONENT P12 — geometry summary ("SL2616 - 3mm Grn LED v003"; no construction recipe available for this part):
  bounding box: 24.0 x 9.2 x 8.0 mm
  tessellated surface: 7,328 triangles
  volume: 406 mm^3 (23% of its bounding box)
  symmetry: 2-fold rotationally symmetric about the y axis; mirror-symmetric across its x mid-plane, z mid-plane
COMPONENT P13 — geometry summary ("MIDI Connector002"; no construction recipe available for this part):
  bounding box: 28.0 x 20.6 x 19.0 mm
  tessellated surface: 59,036 triangles
  volume: 2094 mm^3 (19% of its bounding box)
COMPONENT P14 — geometry summary ("SL2616 - 3mm Grn LED v004"; no construction recipe available for this part):
  bounding box: 24.0 x 9.2 x 8.0 mm
  tessellated surface: 7,328 triangles
  volume: 406 mm^3 (23% of its bounding box)
  symmetry: 2-fold rotationally symmetric about the y axis; mirror-symmetric across its x mid-plane, z mid-plane
COMPONENT P15 — geometry summary ("Boards"; no construction recipe available for this part):
  bounding box: 93.6 x 80.5 x 23.4 mm
  tessellated surface: 115,284 triangles
  volume: 18534 mm^3 (11% of its bounding box)
COMPONENT P16 — recipe-attached ("Raspberry", modeled in this document).
Construction recipe (the document's own serialized feature program — sketch geometry with constraints, then the solid features built on it; lengths are millimeters unless a unit is written):

FEATURE [PartDesign::Plane] DatumPlane002
  AttachmentOffset = pos=(0,0,10) rot=(0,0,1;0rad)
  Length = 110.392
  MapMode = 5
  Placement = pos=(0,0,10) rot=(0,0,1;0rad)
  ResizeMode = 0
  Support = -> [XY_Plane040]
  Width = 63.8924
FEATURE [Sketcher::SketchObject] Sketch011
  FullyConstrained = true
  MapMode = 5
  Placement = pos=(0,0,10) rot=(0,0,1;0rad)
  Support = -> [DatumPlane002]
  sketch-geometry (12):
    g0: LineSegment StartX=32 StartY=7.5 StartZ=0 EndX=32 EndY=-7.5 EndZ=0
    g1: LineSegment StartX=32 StartY=-7.5 StartZ=0 EndX=52 EndY=-7.5 EndZ=0
    g2: LineSegment StartX=52 StartY=-7.5 StartZ=0 EndX=53.5 EndY=-6 EndZ=0
    g3: LineSegment StartX=53.5 StartY=-6 StartZ=0 EndX=62.5 EndY=-6 EndZ=0
    g4: LineSegment StartX=62.5 StartY=-6 StartZ=0 EndX=62.5 EndY=-4 EndZ=0
    g5: LineSegment StartX=62.5 StartY=-4 StartZ=0 EndX=71.5 EndY=-4 EndZ=0
    g6: LineSegment StartX=71.5 StartY=-4 StartZ=0 EndX=71.5 EndY=4 EndZ=0
    g7: LineSegment StartX=71.5 StartY=4 StartZ=0 EndX=62.5 EndY=4 EndZ=0
    g8: LineSegment StartX=62.5 StartY=4 StartZ=0 EndX=62.5 EndY=6 EndZ=0
    g9: LineSegment StartX=62.5 StartY=6 StartZ=0 EndX=53.5 EndY=6 EndZ=0
    g10: LineSegment StartX=53.5 StartY=6 StartZ=0 EndX=52 EndY=7.5 EndZ=0
    g11: LineSegment StartX=52 StartY=7.5 StartZ=0 EndX=32 EndY=7.5 EndZ=0
  constraints (34):
    c: Coincident(g0,g1)
    c: Horizontal(g1)
    c: Coincident(g1,g2)
    c: Coincident(g2,g3)
    c: Horizontal(g3)
    c: Coincident(g3,g4)
    c: Vertical(g4)
    c: Coincident(g4,g5)
    c: Horizontal(g5)
    c: Coincident(g5,g6)
    c: Vertical(g6)
    c: Coincident(g6,g7)
    c: Horizontal(g7)
    c: Coincident(g7,g8)
    c: Coincident(g8,g9)
    c: Horizontal(g9)
    c: Coincident(g9,g10)
    c: Coincident(g10,g11)
    c: Coincident(g11,g0)
    c: Horizontal(g11)
    c: Vertical(g8)
    c: Vertical(g7,g4)
    c: Vertical(g1,g10)
    c: Equal(g8,g4)
    c: DistanceY(g0,g0) = 15
    c: DistanceX(g7,g7) = 9
    c: DistanceY(g6,g6) = 8
    c: DistanceY(g3,g8) = 12
    c: DistanceX(g11,g11) = 20
    c: DistanceX(g0,g3) = 30.5
    c: Angle(g11,g10) = 2.35619
    c: Symmetric(g0,g0,g-1)
    c: Symmetric(g2,g9,g-1)
    c: DistanceX(g-1,g0) = 32
FEATURE [PartDesign::Pad] Pad005
  Direction = (0,0,1)
  Length = 16
  Length2 = 10
  Midplane = true
  Placement = pos=(0,0,10) rot=(0,0,1;0rad)
  Profile = -> Sketch011
  ReferenceAxis = -> Sketch011 [N_Axis]
  Type = 0
FEATURE [PartDesign::Body] Body008  label="USB Connector"
  Group = -> [DatumPlane002,Sketch011,Pad005]
  Origin = -> Origin040
  Placement = pos=(0,-18.5,0) rot=(0,0,1;0rad)
  Tip = -> Pad005
FEATURE [PartDesign::FeatureBase] Clone004
  BaseFeature = -> Body008
FEATURE [PartDesign::Body] Body009  label="USB Connector 2"
  Group = -> [Clone004]
  Origin = -> Origin041
  Placement = pos=(0,-0.5,0) rot=(0,0,1;0rad)
  Tip = -> Clone004
COMPONENT P17 — geometry summary ("Display Group"; no construction recipe available for this part):
  bounding box: 285.0 x 110.8 x 32.4 mm
  tessellated surface: 152,552 triangles
  volume: 154595 mm^3 (15% of its bounding box)
COMPONENT P18 — geometry summary ("MIDI Connectors"; no construction recipe available for this part):
  bounding box: 119.5 x 24.0 x 19.0 mm
  tessellated surface: 265,456 triangles
  volume: 10002 mm^3 (18% of its bounding box)
PROVENANCE & LICENSES
A FreeCAD (.FCStd) document from a public repository crawl; recipes are the document's own serialized feature recipes (and, for linked parts, companion documents' recipes).
License: cc-by-sa-4.0.
